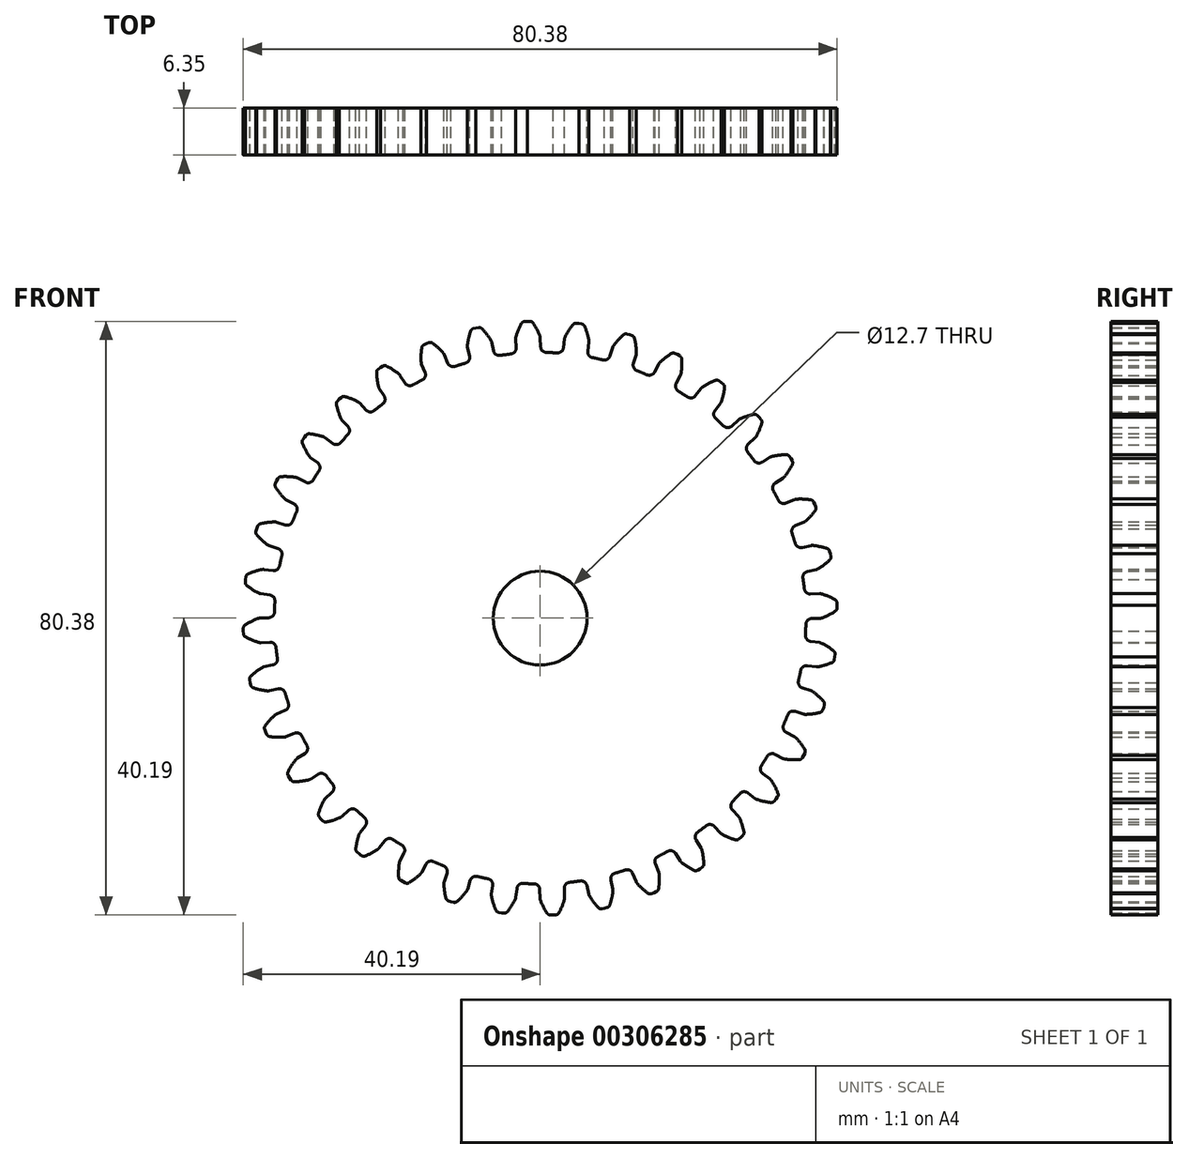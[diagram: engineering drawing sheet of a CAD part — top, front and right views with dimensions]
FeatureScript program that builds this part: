
annotation { "Feature Type Name" : "Feature", "Feature Type Description" : "" }
export const myFeature = defineFeature(function(context is Context, id is Id, definition is map)
    precondition{}
    {
        {
            var Q0;
            Q0=qCreatedBy(makeId("Front.planeOp"),FACE);
            var sketch = newSketch(context, id + "F0", { "sketchPlane" : qUnion([Q0])});
            skArc(sketch, "E0", {"start": v(-3.97, 35.76) * mm, "mid": v(1.57, -35.94) * mm, "end": v(0.84, 35.97) * mm});
            skArc(sketch, "E1.trimOffspring", {"start": v(-0.05, 38.23) * mm, "mid": v(-0.46, 39.12) * mm, "end": v(-0.95, 39.96) * mm});
            skLineSegment(sketch, "E2", {"start": v(-1.38, 40.2) * mm, "end": v(-1.75, 40.2) * mm});
            skLineSegment(sketch, "E3", {"start": v(0, 37.97) * mm, "end": v(0.06, 36.73) * mm});
            skLineSegment(sketch, "E4.MirrorCS", {"start": v(-2.13, 40.16) * mm, "end": v(-1.75, 40.2) * mm});
            skArc(sketch, "E5.MirrorCS", {"start": v(-3.28, 38.09) * mm, "mid": v(-2.96, 39.01) * mm, "end": v(-2.54, 39.9) * mm});
            skLineSegment(sketch, "E6.MirrorCS", {"start": v(-3.31, 37.82) * mm, "end": v(-3.26, 36.59) * mm});
            skPoint(sketch, "E7.visualSharp", {"position": v(-3.23, 35.83) * mm});
            skArc(sketch, "E7.filletArc", {"start": v(-3.97, 35.76) * mm, "mid": v(-3.45, 36.03) * mm, "end": v(-3.26, 36.59) * mm});
            skPoint(sketch, "E8.visualSharp", {"position": v(0.1, 35.98) * mm});
            skArc(sketch, "E8.filletArc", {"start": v(0.06, 36.73) * mm, "mid": v(0.3, 36.2) * mm, "end": v(0.84, 35.97) * mm});
            skPoint(sketch, "E9.visualSharp", {"position": v(0, 38.1) * mm});
            skArc(sketch, "E9.filletArc", {"start": v(0, 37.97) * mm, "mid": v(-0.01, 38.1) * mm, "end": v(-0.05, 38.23) * mm});
            skPoint(sketch, "E10.visualSharp", {"position": v(-3.32, 37.96) * mm});
            skArc(sketch, "E10.filletArc", {"start": v(-3.28, 38.09) * mm, "mid": v(-3.3, 37.96) * mm, "end": v(-3.31, 37.82) * mm});
            skPoint(sketch, "E11.visualSharp", {"position": v(-1.1, 40.2) * mm});
            skArc(sketch, "E11.filletArc", {"start": v(-0.95, 39.96) * mm, "mid": v(-1.13, 40.13) * mm, "end": v(-1.38, 40.2) * mm});
            skPoint(sketch, "E12.visualSharp", {"position": v(-2.4, 40.14) * mm});
            skArc(sketch, "E12.filletArc", {"start": v(-2.13, 40.16) * mm, "mid": v(-2.37, 40.08) * mm, "end": v(-2.54, 39.9) * mm});
            skLineSegment(sketch, "E13.1.0", {"start": v(-9.83, 36.67) * mm, "end": v(-9.57, 35.47) * mm});
            skArc(sketch, "E13.1.1", {"start": v(-9.85, 36.94) * mm, "mid": v(-9.68, 37.9) * mm, "end": v(-9.42, 38.85) * mm});
            skPoint(sketch, "E13.1.2", {"position": v(-6.16, 35.45) * mm});
            skLineSegment(sketch, "E13.1.3", {"start": v(-6.59, 37.4) * mm, "end": v(-6.32, 36.19) * mm});
            skPoint(sketch, "E13.1.4", {"position": v(-9.86, 36.8) * mm});
            skPoint(sketch, "E13.1.5", {"position": v(-9.4, 34.73) * mm});
            skPoint(sketch, "E13.1.6", {"position": v(-8.07, 39.4) * mm});
            skArc(sketch, "E13.1.7", {"start": v(-6.69, 37.64) * mm, "mid": v(-7.24, 38.45) * mm, "end": v(-7.88, 39.2) * mm});
            skPoint(sketch, "E13.1.8", {"position": v(-6.62, 37.52) * mm});
            skPoint(sketch, "E13.1.9", {"position": v(-9.33, 39.1) * mm});
            skArc(sketch, "E13.1.10", {"start": v(-6.32, 36.19) * mm, "mid": v(-6, 35.7) * mm, "end": v(-5.42, 35.57) * mm});
            skArc(sketch, "E13.1.11", {"start": v(-10.12, 34.53) * mm, "mid": v(-9.66, 34.89) * mm, "end": v(-9.57, 35.47) * mm});
            skArc(sketch, "E13.1.12", {"start": v(-7.88, 39.2) * mm, "mid": v(-8.09, 39.33) * mm, "end": v(-8.33, 39.34) * mm});
            skLineSegment(sketch, "E13.1.13", {"start": v(-8.33, 39.34) * mm, "end": v(-8.7, 39.28) * mm});
            skLineSegment(sketch, "E13.1.14", {"start": v(-9.07, 39.18) * mm, "end": v(-8.7, 39.28) * mm});
            skArc(sketch, "E13.1.15", {"start": v(-6.59, 37.4) * mm, "mid": v(-6.63, 37.52) * mm, "end": v(-6.69, 37.64) * mm});
            skArc(sketch, "E13.1.16", {"start": v(-9.85, 36.94) * mm, "mid": v(-9.85, 36.8) * mm, "end": v(-9.83, 36.67) * mm});
            skArc(sketch, "E13.1.17", {"start": v(-9.07, 39.18) * mm, "mid": v(-9.3, 39.06) * mm, "end": v(-9.42, 38.85) * mm});
            skLineSegment(sketch, "E13.2.0", {"start": v(-16.05, 34.4) * mm, "end": v(-15.58, 33.27) * mm});
            skArc(sketch, "E13.2.1", {"start": v(-16.11, 34.67) * mm, "mid": v(-16.12, 35.65) * mm, "end": v(-16.03, 36.62) * mm});
            skPoint(sketch, "E13.2.2", {"position": v(-12.22, 33.84) * mm});
            skLineSegment(sketch, "E13.2.3", {"start": v(-12.98, 35.68) * mm, "end": v(-12.5, 34.54) * mm});
            skPoint(sketch, "E13.2.4", {"position": v(-16.1, 34.53) * mm});
            skPoint(sketch, "E13.2.5", {"position": v(-15.29, 32.57) * mm});
            skPoint(sketch, "E13.2.6", {"position": v(-14.79, 37.4) * mm});
            skArc(sketch, "E13.2.7", {"start": v(-13.12, 35.9) * mm, "mid": v(-13.8, 36.6) * mm, "end": v(-14.56, 37.23) * mm});
            skPoint(sketch, "E13.2.8", {"position": v(-13.03, 35.8) * mm});
            skPoint(sketch, "E13.2.9", {"position": v(-15.98, 36.9) * mm});
            skArc(sketch, "E13.2.10", {"start": v(-12.5, 34.54) * mm, "mid": v(-12.1, 34.12) * mm, "end": v(-11.51, 34.09) * mm});
            skArc(sketch, "E13.2.11", {"start": v(-15.96, 32.24) * mm, "mid": v(-15.57, 32.68) * mm, "end": v(-15.58, 33.27) * mm});
            skArc(sketch, "E13.2.12", {"start": v(-14.56, 37.23) * mm, "mid": v(-14.8, 37.32) * mm, "end": v(-15.04, 37.3) * mm});
            skLineSegment(sketch, "E13.2.13", {"start": v(-15.04, 37.3) * mm, "end": v(-15.4, 37.17) * mm});
            skLineSegment(sketch, "E13.2.14", {"start": v(-15.74, 37) * mm, "end": v(-15.4, 37.17) * mm});
            skArc(sketch, "E13.2.15", {"start": v(-12.98, 35.68) * mm, "mid": v(-13.04, 35.8) * mm, "end": v(-13.12, 35.9) * mm});
            skArc(sketch, "E13.2.16", {"start": v(-16.11, 34.67) * mm, "mid": v(-16.1, 34.54) * mm, "end": v(-16.05, 34.4) * mm});
            skArc(sketch, "E13.2.17", {"start": v(-15.74, 37) * mm, "mid": v(-15.93, 36.85) * mm, "end": v(-16.03, 36.62) * mm});
            skLineSegment(sketch, "E13.3.0", {"start": v(-21.78, 31.1) * mm, "end": v(-21.12, 30.06) * mm});
            skArc(sketch, "E13.3.1", {"start": v(-21.89, 31.34) * mm, "mid": v(-22.06, 32.3) * mm, "end": v(-22.14, 33.28) * mm});
            skPoint(sketch, "E13.3.2", {"position": v(-17.9, 31.2) * mm});
            skLineSegment(sketch, "E13.3.3", {"start": v(-18.98, 32.88) * mm, "end": v(-18.32, 31.84) * mm});
            skPoint(sketch, "E13.3.4", {"position": v(-21.85, 31.2) * mm});
            skPoint(sketch, "E13.3.5", {"position": v(-20.71, 29.42) * mm});
            skPoint(sketch, "E13.3.6", {"position": v(-21.05, 34.25) * mm});
            skArc(sketch, "E13.3.7", {"start": v(-19.16, 33.08) * mm, "mid": v(-19.95, 33.65) * mm, "end": v(-20.8, 34.13) * mm});
            skPoint(sketch, "E13.3.8", {"position": v(-19.05, 33) * mm});
            skPoint(sketch, "E13.3.9", {"position": v(-22.15, 33.56) * mm});
            skArc(sketch, "E13.3.10", {"start": v(-18.32, 31.84) * mm, "mid": v(-17.84, 31.5) * mm, "end": v(-17.26, 31.57) * mm});
            skArc(sketch, "E13.3.11", {"start": v(-21.32, 28.98) * mm, "mid": v(-21, 29.48) * mm, "end": v(-21.12, 30.06) * mm});
            skArc(sketch, "E13.3.12", {"start": v(-20.8, 34.13) * mm, "mid": v(-21.05, 34.19) * mm, "end": v(-21.29, 34.12) * mm});
            skLineSegment(sketch, "E13.3.13", {"start": v(-21.29, 34.12) * mm, "end": v(-21.62, 33.93) * mm});
            skLineSegment(sketch, "E13.3.14", {"start": v(-21.93, 33.71) * mm, "end": v(-21.62, 33.93) * mm});
            skArc(sketch, "E13.3.15", {"start": v(-18.98, 32.88) * mm, "mid": v(-19.06, 33) * mm, "end": v(-19.16, 33.08) * mm});
            skArc(sketch, "E13.3.16", {"start": v(-21.89, 31.34) * mm, "mid": v(-21.84, 31.22) * mm, "end": v(-21.78, 31.1) * mm});
            skArc(sketch, "E13.3.17", {"start": v(-21.93, 33.71) * mm, "mid": v(-22.09, 33.52) * mm, "end": v(-22.14, 33.28) * mm});
            skLineSegment(sketch, "E13.4.0", {"start": v(-26.85, 26.84) * mm, "end": v(-26.02, 25.93) * mm});
            skArc(sketch, "E13.4.1", {"start": v(-27, 27.07) * mm, "mid": v(-27.34, 27.98) * mm, "end": v(-27.59, 28.93) * mm});
            skPoint(sketch, "E13.4.2", {"position": v(-23.06, 27.62) * mm});
            skLineSegment(sketch, "E13.4.3", {"start": v(-24.4, 29.09) * mm, "end": v(-23.57, 28.18) * mm});
            skPoint(sketch, "E13.4.4", {"position": v(-26.94, 26.94) * mm});
            skPoint(sketch, "E13.4.5", {"position": v(-25.5, 25.38) * mm});
            skPoint(sketch, "E13.4.6", {"position": v(-26.68, 30.08) * mm});
            skArc(sketch, "E13.4.7", {"start": v(-24.61, 29.25) * mm, "mid": v(-25.5, 29.67) * mm, "end": v(-26.42, 30) * mm});
            skPoint(sketch, "E13.4.8", {"position": v(-24.5, 29.19) * mm});
            skPoint(sketch, "E13.4.9", {"position": v(-27.64, 29.2) * mm});
            skArc(sketch, "E13.4.10", {"start": v(-23.57, 28.18) * mm, "mid": v(-23.04, 27.92) * mm, "end": v(-22.48, 28.1) * mm});
            skArc(sketch, "E13.4.11", {"start": v(-26.03, 24.84) * mm, "mid": v(-25.8, 25.38) * mm, "end": v(-26.02, 25.93) * mm});
            skArc(sketch, "E13.4.12", {"start": v(-26.42, 30) * mm, "mid": v(-26.67, 30.01) * mm, "end": v(-26.89, 29.9) * mm});
            skLineSegment(sketch, "E13.4.13", {"start": v(-26.89, 29.9) * mm, "end": v(-27.18, 29.66) * mm});
            skLineSegment(sketch, "E13.4.14", {"start": v(-27.45, 29.4) * mm, "end": v(-27.18, 29.66) * mm});
            skArc(sketch, "E13.4.15", {"start": v(-24.4, 29.09) * mm, "mid": v(-24.5, 29.18) * mm, "end": v(-24.61, 29.25) * mm});
            skArc(sketch, "E13.4.16", {"start": v(-27, 27.07) * mm, "mid": v(-26.93, 26.95) * mm, "end": v(-26.85, 26.84) * mm});
            skArc(sketch, "E13.4.17", {"start": v(-27.45, 29.4) * mm, "mid": v(-27.58, 29.18) * mm, "end": v(-27.59, 28.93) * mm});
            skLineSegment(sketch, "E13.5.0", {"start": v(-31.1, 21.77) * mm, "end": v(-30.13, 21.02) * mm});
            skArc(sketch, "E13.5.1", {"start": v(-31.29, 21.97) * mm, "mid": v(-31.78, 22.81) * mm, "end": v(-32.2, 23.7) * mm});
            skPoint(sketch, "E13.5.2", {"position": v(-27.5, 23.2) * mm});
            skLineSegment(sketch, "E13.5.3", {"start": v(-29.08, 24.41) * mm, "end": v(-28.1, 23.66) * mm});
            skPoint(sketch, "E13.5.4", {"position": v(-31.2, 21.85) * mm});
            skPoint(sketch, "E13.5.5", {"position": v(-29.53, 20.56) * mm});
            skPoint(sketch, "E13.5.6", {"position": v(-31.5, 24.99) * mm});
            skArc(sketch, "E13.5.7", {"start": v(-29.32, 24.53) * mm, "mid": v(-30.26, 24.8) * mm, "end": v(-31.23, 24.96) * mm});
            skPoint(sketch, "E13.5.8", {"position": v(-29.19, 24.5) * mm});
            skPoint(sketch, "E13.5.9", {"position": v(-32.29, 23.96) * mm});
            skArc(sketch, "E13.5.10", {"start": v(-28.1, 23.66) * mm, "mid": v(-27.54, 23.5) * mm, "end": v(-27.01, 23.76) * mm});
            skArc(sketch, "E13.5.11", {"start": v(-29.95, 19.94) * mm, "mid": v(-29.82, 20.52) * mm, "end": v(-30.13, 21.02) * mm});
            skArc(sketch, "E13.5.12", {"start": v(-31.23, 24.96) * mm, "mid": v(-31.47, 24.93) * mm, "end": v(-31.67, 24.78) * mm});
            skLineSegment(sketch, "E13.5.13", {"start": v(-31.67, 24.78) * mm, "end": v(-31.92, 24.5) * mm});
            skLineSegment(sketch, "E13.5.14", {"start": v(-32.14, 24.18) * mm, "end": v(-31.92, 24.5) * mm});
            skArc(sketch, "E13.5.15", {"start": v(-29.08, 24.41) * mm, "mid": v(-29.2, 24.48) * mm, "end": v(-29.32, 24.53) * mm});
            skArc(sketch, "E13.5.16", {"start": v(-31.29, 21.97) * mm, "mid": v(-31.2, 21.86) * mm, "end": v(-31.1, 21.77) * mm});
            skArc(sketch, "E13.5.17", {"start": v(-32.14, 24.18) * mm, "mid": v(-32.22, 23.95) * mm, "end": v(-32.2, 23.7) * mm});
            skLineSegment(sketch, "E13.6.0", {"start": v(-34.41, 16.04) * mm, "end": v(-33.32, 15.47) * mm});
            skArc(sketch, "E13.6.1", {"start": v(-34.63, 16.2) * mm, "mid": v(-35.26, 16.95) * mm, "end": v(-35.82, 17.75) * mm});
            skPoint(sketch, "E13.6.2", {"position": v(-31.11, 18.07) * mm});
            skLineSegment(sketch, "E13.6.3", {"start": v(-32.88, 18.99) * mm, "end": v(-31.78, 18.42) * mm});
            skPoint(sketch, "E13.6.4", {"position": v(-34.53, 16.1) * mm});
            skPoint(sketch, "E13.6.5", {"position": v(-32.65, 15.12) * mm});
            skPoint(sketch, "E13.6.6", {"position": v(-35.36, 19.14) * mm});
            skArc(sketch, "E13.6.7", {"start": v(-33.13, 19.07) * mm, "mid": v(-34.1, 19.17) * mm, "end": v(-35.09, 19.16) * mm});
            skPoint(sketch, "E13.6.8", {"position": v(-33, 19.05) * mm});
            skPoint(sketch, "E13.6.9", {"position": v(-35.96, 17.99) * mm});
            skArc(sketch, "E13.6.10", {"start": v(-31.78, 18.42) * mm, "mid": v(-31.2, 18.36) * mm, "end": v(-30.73, 18.71) * mm});
            skArc(sketch, "E13.6.11", {"start": v(-32.95, 14.44) * mm, "mid": v(-32.93, 15.03) * mm, "end": v(-33.32, 15.47) * mm});
            skArc(sketch, "E13.6.12", {"start": v(-35.09, 19.16) * mm, "mid": v(-35.32, 19.08) * mm, "end": v(-35.5, 18.9) * mm});
            skLineSegment(sketch, "E13.6.13", {"start": v(-35.5, 18.9) * mm, "end": v(-35.69, 18.58) * mm});
            skLineSegment(sketch, "E13.6.14", {"start": v(-35.85, 18.23) * mm, "end": v(-35.69, 18.58) * mm});
            skArc(sketch, "E13.6.15", {"start": v(-32.88, 18.99) * mm, "mid": v(-33, 19.04) * mm, "end": v(-33.13, 19.07) * mm});
            skArc(sketch, "E13.6.16", {"start": v(-34.63, 16.2) * mm, "mid": v(-34.53, 16.11) * mm, "end": v(-34.41, 16.04) * mm});
            skArc(sketch, "E13.6.17", {"start": v(-35.85, 18.23) * mm, "mid": v(-35.9, 17.99) * mm, "end": v(-35.82, 17.75) * mm});
            skLineSegment(sketch, "E13.7.0", {"start": v(-36.68, 9.82) * mm, "end": v(-35.5, 9.45) * mm});
            skArc(sketch, "E13.7.1", {"start": v(-36.91, 9.94) * mm, "mid": v(-37.67, 10.56) * mm, "end": v(-38.36, 11.26) * mm});
            skPoint(sketch, "E13.7.2", {"position": v(-33.78, 12.4) * mm});
            skLineSegment(sketch, "E13.7.3", {"start": v(-35.68, 13) * mm, "end": v(-34.5, 12.62) * mm});
            skPoint(sketch, "E13.7.4", {"position": v(-36.8, 9.86) * mm});
            skPoint(sketch, "E13.7.5", {"position": v(-34.78, 9.22) * mm});
            skPoint(sketch, "E13.7.6", {"position": v(-38.15, 12.7) * mm});
            skArc(sketch, "E13.7.7", {"start": v(-35.94, 13.03) * mm, "mid": v(-36.92, 12.95) * mm, "end": v(-37.88, 12.77) * mm});
            skPoint(sketch, "E13.7.8", {"position": v(-35.8, 13.03) * mm});
            skPoint(sketch, "E13.7.9", {"position": v(-38.54, 11.47) * mm});
            skArc(sketch, "E13.7.10", {"start": v(-34.5, 12.62) * mm, "mid": v(-33.91, 12.66) * mm, "end": v(-33.51, 13.1) * mm});
            skArc(sketch, "E13.7.11", {"start": v(-34.96, 8.5) * mm, "mid": v(-35.04, 9.08) * mm, "end": v(-35.5, 9.45) * mm});
            skArc(sketch, "E13.7.12", {"start": v(-37.88, 12.77) * mm, "mid": v(-38.1, 12.66) * mm, "end": v(-38.24, 12.45) * mm});
            skLineSegment(sketch, "E13.7.13", {"start": v(-38.24, 12.45) * mm, "end": v(-38.37, 12.1) * mm});
            skLineSegment(sketch, "E13.7.14", {"start": v(-38.47, 11.73) * mm, "end": v(-38.37, 12.1) * mm});
            skArc(sketch, "E13.7.15", {"start": v(-35.68, 13) * mm, "mid": v(-35.8, 13.02) * mm, "end": v(-35.94, 13.03) * mm});
            skArc(sketch, "E13.7.16", {"start": v(-36.91, 9.94) * mm, "mid": v(-36.8, 9.87) * mm, "end": v(-36.68, 9.82) * mm});
            skArc(sketch, "E13.7.17", {"start": v(-38.47, 11.73) * mm, "mid": v(-38.47, 11.48) * mm, "end": v(-38.36, 11.26) * mm});
            skLineSegment(sketch, "E13.8.0", {"start": v(-37.82, 3.3) * mm, "end": v(-36.6, 3.14) * mm});
            skArc(sketch, "E13.8.1", {"start": v(-38.08, 3.38) * mm, "mid": v(-38.93, 3.86) * mm, "end": v(-39.73, 4.43) * mm});
            skPoint(sketch, "E13.8.2", {"position": v(-35.42, 6.34) * mm});
            skLineSegment(sketch, "E13.8.3", {"start": v(-37.4, 6.6) * mm, "end": v(-36.17, 6.44) * mm});
            skPoint(sketch, "E13.8.4", {"position": v(-37.96, 3.32) * mm});
            skPoint(sketch, "E13.8.5", {"position": v(-35.85, 3.04) * mm});
            skPoint(sketch, "E13.8.6", {"position": v(-39.77, 5.89) * mm});
            skArc(sketch, "E13.8.7", {"start": v(-37.66, 6.59) * mm, "mid": v(-38.6, 6.34) * mm, "end": v(-39.52, 6) * mm});
            skPoint(sketch, "E13.8.8", {"position": v(-37.52, 6.62) * mm});
            skPoint(sketch, "E13.8.9", {"position": v(-39.94, 4.6) * mm});
            skArc(sketch, "E13.8.10", {"start": v(-36.17, 6.44) * mm, "mid": v(-35.6, 6.58) * mm, "end": v(-35.28, 7.07) * mm});
            skArc(sketch, "E13.8.11", {"start": v(-35.9, 2.3) * mm, "mid": v(-36.09, 2.86) * mm, "end": v(-36.6, 3.14) * mm});
            skArc(sketch, "E13.8.12", {"start": v(-39.52, 6) * mm, "mid": v(-39.72, 5.85) * mm, "end": v(-39.82, 5.62) * mm});
            skLineSegment(sketch, "E13.8.13", {"start": v(-39.82, 5.62) * mm, "end": v(-39.89, 5.25) * mm});
            skLineSegment(sketch, "E13.8.14", {"start": v(-39.92, 4.87) * mm, "end": v(-39.89, 5.25) * mm});
            skArc(sketch, "E13.8.15", {"start": v(-37.4, 6.6) * mm, "mid": v(-37.52, 6.6) * mm, "end": v(-37.66, 6.59) * mm});
            skArc(sketch, "E13.8.16", {"start": v(-38.08, 3.38) * mm, "mid": v(-37.95, 3.33) * mm, "end": v(-37.82, 3.3) * mm});
            skArc(sketch, "E13.8.17", {"start": v(-39.92, 4.87) * mm, "mid": v(-39.88, 4.63) * mm, "end": v(-39.73, 4.43) * mm});
            skLineSegment(sketch, "E13.9.0", {"start": v(-37.82, -3.31) * mm, "end": v(-36.59, -3.26) * mm});
            skArc(sketch, "E13.9.1", {"start": v(-38.09, -3.28) * mm, "mid": v(-39.01, -2.96) * mm, "end": v(-39.9, -2.54) * mm});
            skPoint(sketch, "E13.9.2", {"position": v(-35.98, 0.1) * mm});
            skLineSegment(sketch, "E13.9.3", {"start": v(-37.97, 0) * mm, "end": v(-36.73, 0.06) * mm});
            skPoint(sketch, "E13.9.4", {"position": v(-37.96, -3.32) * mm});
            skPoint(sketch, "E13.9.5", {"position": v(-35.83, -3.23) * mm});
            skPoint(sketch, "E13.9.6", {"position": v(-40.2, -1.1) * mm});
            skArc(sketch, "E13.9.7", {"start": v(-38.23, -0.05) * mm, "mid": v(-39.12, -0.46) * mm, "end": v(-39.96, -0.95) * mm});
            skPoint(sketch, "E13.9.8", {"position": v(-38.1, 0) * mm});
            skPoint(sketch, "E13.9.9", {"position": v(-40.14, -2.4) * mm});
            skArc(sketch, "E13.9.10", {"start": v(-36.73, 0.06) * mm, "mid": v(-36.2, 0.3) * mm, "end": v(-35.97, 0.84) * mm});
            skArc(sketch, "E13.9.11", {"start": v(-35.76, -3.97) * mm, "mid": v(-36.03, -3.45) * mm, "end": v(-36.59, -3.26) * mm});
            skArc(sketch, "E13.9.12", {"start": v(-39.96, -0.95) * mm, "mid": v(-40.13, -1.13) * mm, "end": v(-40.2, -1.38) * mm});
            skLineSegment(sketch, "E13.9.13", {"start": v(-40.2, -1.38) * mm, "end": v(-40.2, -1.75) * mm});
            skLineSegment(sketch, "E13.9.14", {"start": v(-40.16, -2.13) * mm, "end": v(-40.2, -1.75) * mm});
            skArc(sketch, "E13.9.15", {"start": v(-37.97, 0) * mm, "mid": v(-38.1, -0.01) * mm, "end": v(-38.23, -0.05) * mm});
            skArc(sketch, "E13.9.16", {"start": v(-38.09, -3.28) * mm, "mid": v(-37.96, -3.3) * mm, "end": v(-37.82, -3.31) * mm});
            skArc(sketch, "E13.9.17", {"start": v(-40.16, -2.13) * mm, "mid": v(-40.08, -2.37) * mm, "end": v(-39.9, -2.54) * mm});
            skLineSegment(sketch, "E13.10.0", {"start": v(-36.67, -9.83) * mm, "end": v(-35.47, -9.57) * mm});
            skArc(sketch, "E13.10.1", {"start": v(-36.94, -9.85) * mm, "mid": v(-37.9, -9.68) * mm, "end": v(-38.85, -9.42) * mm});
            skPoint(sketch, "E13.10.2", {"position": v(-35.45, -6.16) * mm});
            skLineSegment(sketch, "E13.10.3", {"start": v(-37.4, -6.59) * mm, "end": v(-36.19, -6.32) * mm});
            skPoint(sketch, "E13.10.4", {"position": v(-36.8, -9.86) * mm});
            skPoint(sketch, "E13.10.5", {"position": v(-34.73, -9.4) * mm});
            skPoint(sketch, "E13.10.6", {"position": v(-39.4, -8.07) * mm});
            skArc(sketch, "E13.10.7", {"start": v(-37.64, -6.69) * mm, "mid": v(-38.45, -7.24) * mm, "end": v(-39.2, -7.88) * mm});
            skPoint(sketch, "E13.10.8", {"position": v(-37.52, -6.62) * mm});
            skPoint(sketch, "E13.10.9", {"position": v(-39.1, -9.33) * mm});
            skArc(sketch, "E13.10.10", {"start": v(-36.19, -6.32) * mm, "mid": v(-35.7, -6) * mm, "end": v(-35.57, -5.42) * mm});
            skArc(sketch, "E13.10.11", {"start": v(-34.53, -10.12) * mm, "mid": v(-34.89, -9.66) * mm, "end": v(-35.47, -9.57) * mm});
            skArc(sketch, "E13.10.12", {"start": v(-39.2, -7.88) * mm, "mid": v(-39.33, -8.09) * mm, "end": v(-39.34, -8.33) * mm});
            skLineSegment(sketch, "E13.10.13", {"start": v(-39.34, -8.33) * mm, "end": v(-39.28, -8.7) * mm});
            skLineSegment(sketch, "E13.10.14", {"start": v(-39.18, -9.07) * mm, "end": v(-39.28, -8.7) * mm});
            skArc(sketch, "E13.10.15", {"start": v(-37.4, -6.59) * mm, "mid": v(-37.52, -6.63) * mm, "end": v(-37.64, -6.69) * mm});
            skArc(sketch, "E13.10.16", {"start": v(-36.94, -9.85) * mm, "mid": v(-36.8, -9.85) * mm, "end": v(-36.67, -9.83) * mm});
            skArc(sketch, "E13.10.17", {"start": v(-39.18, -9.07) * mm, "mid": v(-39.06, -9.3) * mm, "end": v(-38.85, -9.42) * mm});
            skLineSegment(sketch, "E13.11.0", {"start": v(-34.4, -16.05) * mm, "end": v(-33.27, -15.58) * mm});
            skArc(sketch, "E13.11.1", {"start": v(-34.67, -16.11) * mm, "mid": v(-35.65, -16.12) * mm, "end": v(-36.62, -16.03) * mm});
            skPoint(sketch, "E13.11.2", {"position": v(-33.84, -12.22) * mm});
            skLineSegment(sketch, "E13.11.3", {"start": v(-35.68, -12.98) * mm, "end": v(-34.54, -12.5) * mm});
            skPoint(sketch, "E13.11.4", {"position": v(-34.53, -16.1) * mm});
            skPoint(sketch, "E13.11.5", {"position": v(-32.57, -15.29) * mm});
            skPoint(sketch, "E13.11.6", {"position": v(-37.4, -14.79) * mm});
            skArc(sketch, "E13.11.7", {"start": v(-35.9, -13.12) * mm, "mid": v(-36.6, -13.8) * mm, "end": v(-37.23, -14.56) * mm});
            skPoint(sketch, "E13.11.8", {"position": v(-35.8, -13.03) * mm});
            skPoint(sketch, "E13.11.9", {"position": v(-36.9, -15.98) * mm});
            skArc(sketch, "E13.11.10", {"start": v(-34.54, -12.5) * mm, "mid": v(-34.12, -12.1) * mm, "end": v(-34.09, -11.51) * mm});
            skArc(sketch, "E13.11.11", {"start": v(-32.24, -15.96) * mm, "mid": v(-32.68, -15.57) * mm, "end": v(-33.27, -15.58) * mm});
            skArc(sketch, "E13.11.12", {"start": v(-37.23, -14.56) * mm, "mid": v(-37.32, -14.8) * mm, "end": v(-37.3, -15.04) * mm});
            skLineSegment(sketch, "E13.11.13", {"start": v(-37.3, -15.04) * mm, "end": v(-37.17, -15.4) * mm});
            skLineSegment(sketch, "E13.11.14", {"start": v(-37, -15.74) * mm, "end": v(-37.17, -15.4) * mm});
            skArc(sketch, "E13.11.15", {"start": v(-35.68, -12.98) * mm, "mid": v(-35.8, -13.04) * mm, "end": v(-35.9, -13.12) * mm});
            skArc(sketch, "E13.11.16", {"start": v(-34.67, -16.11) * mm, "mid": v(-34.54, -16.1) * mm, "end": v(-34.4, -16.05) * mm});
            skArc(sketch, "E13.11.17", {"start": v(-37, -15.74) * mm, "mid": v(-36.85, -15.93) * mm, "end": v(-36.62, -16.03) * mm});
            skLineSegment(sketch, "E13.12.0", {"start": v(-31.1, -21.78) * mm, "end": v(-30.06, -21.12) * mm});
            skArc(sketch, "E13.12.1", {"start": v(-31.34, -21.89) * mm, "mid": v(-32.3, -22.06) * mm, "end": v(-33.28, -22.14) * mm});
            skPoint(sketch, "E13.12.2", {"position": v(-31.2, -17.9) * mm});
            skLineSegment(sketch, "E13.12.3", {"start": v(-32.88, -18.98) * mm, "end": v(-31.84, -18.32) * mm});
            skPoint(sketch, "E13.12.4", {"position": v(-31.2, -21.85) * mm});
            skPoint(sketch, "E13.12.5", {"position": v(-29.42, -20.71) * mm});
            skPoint(sketch, "E13.12.6", {"position": v(-34.25, -21.05) * mm});
            skArc(sketch, "E13.12.7", {"start": v(-33.08, -19.16) * mm, "mid": v(-33.65, -19.95) * mm, "end": v(-34.13, -20.8) * mm});
            skPoint(sketch, "E13.12.8", {"position": v(-33, -19.05) * mm});
            skPoint(sketch, "E13.12.9", {"position": v(-33.56, -22.15) * mm});
            skArc(sketch, "E13.12.10", {"start": v(-31.84, -18.32) * mm, "mid": v(-31.5, -17.84) * mm, "end": v(-31.57, -17.26) * mm});
            skArc(sketch, "E13.12.11", {"start": v(-28.98, -21.32) * mm, "mid": v(-29.48, -21) * mm, "end": v(-30.06, -21.12) * mm});
            skArc(sketch, "E13.12.12", {"start": v(-34.13, -20.8) * mm, "mid": v(-34.19, -21.05) * mm, "end": v(-34.12, -21.29) * mm});
            skLineSegment(sketch, "E13.12.13", {"start": v(-34.12, -21.29) * mm, "end": v(-33.93, -21.62) * mm});
            skLineSegment(sketch, "E13.12.14", {"start": v(-33.71, -21.93) * mm, "end": v(-33.93, -21.62) * mm});
            skArc(sketch, "E13.12.15", {"start": v(-32.88, -18.98) * mm, "mid": v(-33, -19.06) * mm, "end": v(-33.08, -19.16) * mm});
            skArc(sketch, "E13.12.16", {"start": v(-31.34, -21.89) * mm, "mid": v(-31.22, -21.84) * mm, "end": v(-31.1, -21.78) * mm});
            skArc(sketch, "E13.12.17", {"start": v(-33.71, -21.93) * mm, "mid": v(-33.52, -22.09) * mm, "end": v(-33.28, -22.14) * mm});
            skLineSegment(sketch, "E13.13.0", {"start": v(-26.84, -26.85) * mm, "end": v(-25.93, -26.02) * mm});
            skArc(sketch, "E13.13.1", {"start": v(-27.07, -27) * mm, "mid": v(-27.98, -27.34) * mm, "end": v(-28.93, -27.59) * mm});
            skPoint(sketch, "E13.13.2", {"position": v(-27.62, -23.06) * mm});
            skLineSegment(sketch, "E13.13.3", {"start": v(-29.09, -24.4) * mm, "end": v(-28.18, -23.57) * mm});
            skPoint(sketch, "E13.13.4", {"position": v(-26.94, -26.94) * mm});
            skPoint(sketch, "E13.13.5", {"position": v(-25.38, -25.5) * mm});
            skPoint(sketch, "E13.13.6", {"position": v(-30.08, -26.68) * mm});
            skArc(sketch, "E13.13.7", {"start": v(-29.25, -24.61) * mm, "mid": v(-29.67, -25.5) * mm, "end": v(-30, -26.42) * mm});
            skPoint(sketch, "E13.13.8", {"position": v(-29.19, -24.5) * mm});
            skPoint(sketch, "E13.13.9", {"position": v(-29.2, -27.64) * mm});
            skArc(sketch, "E13.13.10", {"start": v(-28.18, -23.57) * mm, "mid": v(-27.92, -23.04) * mm, "end": v(-28.1, -22.48) * mm});
            skArc(sketch, "E13.13.11", {"start": v(-24.84, -26.03) * mm, "mid": v(-25.38, -25.8) * mm, "end": v(-25.93, -26.02) * mm});
            skArc(sketch, "E13.13.12", {"start": v(-30, -26.42) * mm, "mid": v(-30.01, -26.67) * mm, "end": v(-29.9, -26.89) * mm});
            skLineSegment(sketch, "E13.13.13", {"start": v(-29.9, -26.89) * mm, "end": v(-29.66, -27.18) * mm});
            skLineSegment(sketch, "E13.13.14", {"start": v(-29.4, -27.45) * mm, "end": v(-29.66, -27.18) * mm});
            skArc(sketch, "E13.13.15", {"start": v(-29.09, -24.4) * mm, "mid": v(-29.18, -24.5) * mm, "end": v(-29.25, -24.61) * mm});
            skArc(sketch, "E13.13.16", {"start": v(-27.07, -27) * mm, "mid": v(-26.95, -26.93) * mm, "end": v(-26.84, -26.85) * mm});
            skArc(sketch, "E13.13.17", {"start": v(-29.4, -27.45) * mm, "mid": v(-29.18, -27.58) * mm, "end": v(-28.93, -27.59) * mm});
            skLineSegment(sketch, "E13.14.0", {"start": v(-21.77, -31.1) * mm, "end": v(-21.02, -30.13) * mm});
            skArc(sketch, "E13.14.1", {"start": v(-21.97, -31.29) * mm, "mid": v(-22.81, -31.78) * mm, "end": v(-23.7, -32.2) * mm});
            skPoint(sketch, "E13.14.2", {"position": v(-23.2, -27.5) * mm});
            skLineSegment(sketch, "E13.14.3", {"start": v(-24.41, -29.08) * mm, "end": v(-23.66, -28.1) * mm});
            skPoint(sketch, "E13.14.4", {"position": v(-21.85, -31.2) * mm});
            skPoint(sketch, "E13.14.5", {"position": v(-20.56, -29.53) * mm});
            skPoint(sketch, "E13.14.6", {"position": v(-24.99, -31.5) * mm});
            skArc(sketch, "E13.14.7", {"start": v(-24.53, -29.32) * mm, "mid": v(-24.8, -30.26) * mm, "end": v(-24.96, -31.23) * mm});
            skPoint(sketch, "E13.14.8", {"position": v(-24.5, -29.19) * mm});
            skPoint(sketch, "E13.14.9", {"position": v(-23.96, -32.29) * mm});
            skArc(sketch, "E13.14.10", {"start": v(-23.66, -28.1) * mm, "mid": v(-23.5, -27.54) * mm, "end": v(-23.76, -27.01) * mm});
            skArc(sketch, "E13.14.11", {"start": v(-19.94, -29.95) * mm, "mid": v(-20.52, -29.82) * mm, "end": v(-21.02, -30.13) * mm});
            skArc(sketch, "E13.14.12", {"start": v(-24.96, -31.23) * mm, "mid": v(-24.93, -31.47) * mm, "end": v(-24.78, -31.67) * mm});
            skLineSegment(sketch, "E13.14.13", {"start": v(-24.78, -31.67) * mm, "end": v(-24.5, -31.92) * mm});
            skLineSegment(sketch, "E13.14.14", {"start": v(-24.18, -32.14) * mm, "end": v(-24.5, -31.92) * mm});
            skArc(sketch, "E13.14.15", {"start": v(-24.41, -29.08) * mm, "mid": v(-24.48, -29.2) * mm, "end": v(-24.53, -29.32) * mm});
            skArc(sketch, "E13.14.16", {"start": v(-21.97, -31.29) * mm, "mid": v(-21.86, -31.2) * mm, "end": v(-21.77, -31.1) * mm});
            skArc(sketch, "E13.14.17", {"start": v(-24.18, -32.14) * mm, "mid": v(-23.95, -32.22) * mm, "end": v(-23.7, -32.2) * mm});
            skLineSegment(sketch, "E13.15.0", {"start": v(-16.04, -34.41) * mm, "end": v(-15.47, -33.32) * mm});
            skArc(sketch, "E13.15.1", {"start": v(-16.2, -34.63) * mm, "mid": v(-16.95, -35.26) * mm, "end": v(-17.75, -35.82) * mm});
            skPoint(sketch, "E13.15.2", {"position": v(-18.07, -31.11) * mm});
            skLineSegment(sketch, "E13.15.3", {"start": v(-18.99, -32.88) * mm, "end": v(-18.42, -31.78) * mm});
            skPoint(sketch, "E13.15.4", {"position": v(-16.1, -34.53) * mm});
            skPoint(sketch, "E13.15.5", {"position": v(-15.12, -32.65) * mm});
            skPoint(sketch, "E13.15.6", {"position": v(-19.14, -35.36) * mm});
            skArc(sketch, "E13.15.7", {"start": v(-19.07, -33.13) * mm, "mid": v(-19.17, -34.1) * mm, "end": v(-19.16, -35.09) * mm});
            skPoint(sketch, "E13.15.8", {"position": v(-19.05, -33) * mm});
            skPoint(sketch, "E13.15.9", {"position": v(-17.99, -35.96) * mm});
            skArc(sketch, "E13.15.10", {"start": v(-18.42, -31.78) * mm, "mid": v(-18.36, -31.2) * mm, "end": v(-18.71, -30.73) * mm});
            skArc(sketch, "E13.15.11", {"start": v(-14.44, -32.95) * mm, "mid": v(-15.03, -32.93) * mm, "end": v(-15.47, -33.32) * mm});
            skArc(sketch, "E13.15.12", {"start": v(-19.16, -35.09) * mm, "mid": v(-19.08, -35.32) * mm, "end": v(-18.9, -35.5) * mm});
            skLineSegment(sketch, "E13.15.13", {"start": v(-18.9, -35.5) * mm, "end": v(-18.58, -35.69) * mm});
            skLineSegment(sketch, "E13.15.14", {"start": v(-18.23, -35.85) * mm, "end": v(-18.58, -35.69) * mm});
            skArc(sketch, "E13.15.15", {"start": v(-18.99, -32.88) * mm, "mid": v(-19.04, -33) * mm, "end": v(-19.07, -33.13) * mm});
            skArc(sketch, "E13.15.16", {"start": v(-16.2, -34.63) * mm, "mid": v(-16.11, -34.53) * mm, "end": v(-16.04, -34.41) * mm});
            skArc(sketch, "E13.15.17", {"start": v(-18.23, -35.85) * mm, "mid": v(-17.99, -35.9) * mm, "end": v(-17.75, -35.82) * mm});
            skLineSegment(sketch, "E13.16.0", {"start": v(-9.82, -36.68) * mm, "end": v(-9.45, -35.5) * mm});
            skArc(sketch, "E13.16.1", {"start": v(-9.94, -36.91) * mm, "mid": v(-10.56, -37.67) * mm, "end": v(-11.26, -38.36) * mm});
            skPoint(sketch, "E13.16.2", {"position": v(-12.4, -33.78) * mm});
            skLineSegment(sketch, "E13.16.3", {"start": v(-13, -35.68) * mm, "end": v(-12.62, -34.5) * mm});
            skPoint(sketch, "E13.16.4", {"position": v(-9.86, -36.8) * mm});
            skPoint(sketch, "E13.16.5", {"position": v(-9.22, -34.78) * mm});
            skPoint(sketch, "E13.16.6", {"position": v(-12.7, -38.15) * mm});
            skArc(sketch, "E13.16.7", {"start": v(-13.03, -35.94) * mm, "mid": v(-12.95, -36.92) * mm, "end": v(-12.77, -37.88) * mm});
            skPoint(sketch, "E13.16.8", {"position": v(-13.03, -35.8) * mm});
            skPoint(sketch, "E13.16.9", {"position": v(-11.47, -38.54) * mm});
            skArc(sketch, "E13.16.10", {"start": v(-12.62, -34.5) * mm, "mid": v(-12.66, -33.91) * mm, "end": v(-13.1, -33.51) * mm});
            skArc(sketch, "E13.16.11", {"start": v(-8.5, -34.96) * mm, "mid": v(-9.08, -35.04) * mm, "end": v(-9.45, -35.5) * mm});
            skArc(sketch, "E13.16.12", {"start": v(-12.77, -37.88) * mm, "mid": v(-12.66, -38.1) * mm, "end": v(-12.45, -38.24) * mm});
            skLineSegment(sketch, "E13.16.13", {"start": v(-12.45, -38.24) * mm, "end": v(-12.1, -38.37) * mm});
            skLineSegment(sketch, "E13.16.14", {"start": v(-11.73, -38.47) * mm, "end": v(-12.1, -38.37) * mm});
            skArc(sketch, "E13.16.15", {"start": v(-13, -35.68) * mm, "mid": v(-13.02, -35.8) * mm, "end": v(-13.03, -35.94) * mm});
            skArc(sketch, "E13.16.16", {"start": v(-9.94, -36.91) * mm, "mid": v(-9.87, -36.8) * mm, "end": v(-9.82, -36.68) * mm});
            skArc(sketch, "E13.16.17", {"start": v(-11.73, -38.47) * mm, "mid": v(-11.48, -38.47) * mm, "end": v(-11.26, -38.36) * mm});
            skLineSegment(sketch, "E13.17.0", {"start": v(-3.3, -37.82) * mm, "end": v(-3.14, -36.6) * mm});
            skArc(sketch, "E13.17.1", {"start": v(-3.38, -38.08) * mm, "mid": v(-3.86, -38.93) * mm, "end": v(-4.43, -39.73) * mm});
            skPoint(sketch, "E13.17.2", {"position": v(-6.34, -35.42) * mm});
            skLineSegment(sketch, "E13.17.3", {"start": v(-6.6, -37.4) * mm, "end": v(-6.44, -36.17) * mm});
            skPoint(sketch, "E13.17.4", {"position": v(-3.32, -37.96) * mm});
            skPoint(sketch, "E13.17.5", {"position": v(-3.04, -35.85) * mm});
            skPoint(sketch, "E13.17.6", {"position": v(-5.89, -39.77) * mm});
            skArc(sketch, "E13.17.7", {"start": v(-6.59, -37.66) * mm, "mid": v(-6.34, -38.6) * mm, "end": v(-6, -39.52) * mm});
            skPoint(sketch, "E13.17.8", {"position": v(-6.62, -37.52) * mm});
            skPoint(sketch, "E13.17.9", {"position": v(-4.6, -39.94) * mm});
            skArc(sketch, "E13.17.10", {"start": v(-6.44, -36.17) * mm, "mid": v(-6.58, -35.6) * mm, "end": v(-7.07, -35.28) * mm});
            skArc(sketch, "E13.17.11", {"start": v(-2.3, -35.9) * mm, "mid": v(-2.86, -36.09) * mm, "end": v(-3.14, -36.6) * mm});
            skArc(sketch, "E13.17.12", {"start": v(-6, -39.52) * mm, "mid": v(-5.85, -39.72) * mm, "end": v(-5.62, -39.82) * mm});
            skLineSegment(sketch, "E13.17.13", {"start": v(-5.62, -39.82) * mm, "end": v(-5.25, -39.89) * mm});
            skLineSegment(sketch, "E13.17.14", {"start": v(-4.87, -39.92) * mm, "end": v(-5.25, -39.89) * mm});
            skArc(sketch, "E13.17.15", {"start": v(-6.6, -37.4) * mm, "mid": v(-6.6, -37.52) * mm, "end": v(-6.59, -37.66) * mm});
            skArc(sketch, "E13.17.16", {"start": v(-3.38, -38.08) * mm, "mid": v(-3.33, -37.95) * mm, "end": v(-3.3, -37.82) * mm});
            skArc(sketch, "E13.17.17", {"start": v(-4.87, -39.92) * mm, "mid": v(-4.63, -39.88) * mm, "end": v(-4.43, -39.73) * mm});
            skLineSegment(sketch, "E13.18.0", {"start": v(3.31, -37.82) * mm, "end": v(3.26, -36.59) * mm});
            skArc(sketch, "E13.18.1", {"start": v(3.28, -38.09) * mm, "mid": v(2.96, -39.01) * mm, "end": v(2.54, -39.9) * mm});
            skPoint(sketch, "E13.18.2", {"position": v(-0.1, -35.98) * mm});
            skLineSegment(sketch, "E13.18.3", {"start": v(0, -37.97) * mm, "end": v(-0.06, -36.73) * mm});
            skPoint(sketch, "E13.18.4", {"position": v(3.32, -37.96) * mm});
            skPoint(sketch, "E13.18.5", {"position": v(3.23, -35.83) * mm});
            skPoint(sketch, "E13.18.6", {"position": v(1.1, -40.2) * mm});
            skArc(sketch, "E13.18.7", {"start": v(0.05, -38.23) * mm, "mid": v(0.46, -39.12) * mm, "end": v(0.95, -39.96) * mm});
            skPoint(sketch, "E13.18.8", {"position": v(0, -38.1) * mm});
            skPoint(sketch, "E13.18.9", {"position": v(2.4, -40.14) * mm});
            skArc(sketch, "E13.18.10", {"start": v(-0.06, -36.73) * mm, "mid": v(-0.3, -36.2) * mm, "end": v(-0.84, -35.97) * mm});
            skArc(sketch, "E13.18.11", {"start": v(3.97, -35.76) * mm, "mid": v(3.45, -36.03) * mm, "end": v(3.26, -36.59) * mm});
            skArc(sketch, "E13.18.12", {"start": v(0.95, -39.96) * mm, "mid": v(1.13, -40.13) * mm, "end": v(1.38, -40.2) * mm});
            skLineSegment(sketch, "E13.18.13", {"start": v(1.38, -40.2) * mm, "end": v(1.75, -40.2) * mm});
            skLineSegment(sketch, "E13.18.14", {"start": v(2.13, -40.16) * mm, "end": v(1.75, -40.2) * mm});
            skArc(sketch, "E13.18.15", {"start": v(0, -37.97) * mm, "mid": v(0.01, -38.1) * mm, "end": v(0.05, -38.23) * mm});
            skArc(sketch, "E13.18.16", {"start": v(3.28, -38.09) * mm, "mid": v(3.3, -37.96) * mm, "end": v(3.31, -37.82) * mm});
            skArc(sketch, "E13.18.17", {"start": v(2.13, -40.16) * mm, "mid": v(2.37, -40.08) * mm, "end": v(2.54, -39.9) * mm});
            skLineSegment(sketch, "E13.19.0", {"start": v(9.83, -36.67) * mm, "end": v(9.57, -35.47) * mm});
            skArc(sketch, "E13.19.1", {"start": v(9.85, -36.94) * mm, "mid": v(9.68, -37.9) * mm, "end": v(9.42, -38.85) * mm});
            skPoint(sketch, "E13.19.2", {"position": v(6.16, -35.45) * mm});
            skLineSegment(sketch, "E13.19.3", {"start": v(6.59, -37.4) * mm, "end": v(6.32, -36.19) * mm});
            skPoint(sketch, "E13.19.4", {"position": v(9.86, -36.8) * mm});
            skPoint(sketch, "E13.19.5", {"position": v(9.4, -34.73) * mm});
            skPoint(sketch, "E13.19.6", {"position": v(8.07, -39.4) * mm});
            skArc(sketch, "E13.19.7", {"start": v(6.69, -37.64) * mm, "mid": v(7.24, -38.45) * mm, "end": v(7.88, -39.2) * mm});
            skPoint(sketch, "E13.19.8", {"position": v(6.62, -37.52) * mm});
            skPoint(sketch, "E13.19.9", {"position": v(9.33, -39.1) * mm});
            skArc(sketch, "E13.19.10", {"start": v(6.32, -36.19) * mm, "mid": v(6, -35.7) * mm, "end": v(5.42, -35.57) * mm});
            skArc(sketch, "E13.19.11", {"start": v(10.12, -34.53) * mm, "mid": v(9.66, -34.89) * mm, "end": v(9.57, -35.47) * mm});
            skArc(sketch, "E13.19.12", {"start": v(7.88, -39.2) * mm, "mid": v(8.09, -39.33) * mm, "end": v(8.33, -39.34) * mm});
            skLineSegment(sketch, "E13.19.13", {"start": v(8.33, -39.34) * mm, "end": v(8.7, -39.28) * mm});
            skLineSegment(sketch, "E13.19.14", {"start": v(9.07, -39.18) * mm, "end": v(8.7, -39.28) * mm});
            skArc(sketch, "E13.19.15", {"start": v(6.59, -37.4) * mm, "mid": v(6.63, -37.52) * mm, "end": v(6.69, -37.64) * mm});
            skArc(sketch, "E13.19.16", {"start": v(9.85, -36.94) * mm, "mid": v(9.85, -36.8) * mm, "end": v(9.83, -36.67) * mm});
            skArc(sketch, "E13.19.17", {"start": v(9.07, -39.18) * mm, "mid": v(9.3, -39.06) * mm, "end": v(9.42, -38.85) * mm});
            skLineSegment(sketch, "E13.20.0", {"start": v(16.05, -34.4) * mm, "end": v(15.58, -33.27) * mm});
            skArc(sketch, "E13.20.1", {"start": v(16.11, -34.67) * mm, "mid": v(16.12, -35.65) * mm, "end": v(16.03, -36.62) * mm});
            skPoint(sketch, "E13.20.2", {"position": v(12.22, -33.84) * mm});
            skLineSegment(sketch, "E13.20.3", {"start": v(12.98, -35.68) * mm, "end": v(12.5, -34.54) * mm});
            skPoint(sketch, "E13.20.4", {"position": v(16.1, -34.53) * mm});
            skPoint(sketch, "E13.20.5", {"position": v(15.29, -32.57) * mm});
            skPoint(sketch, "E13.20.6", {"position": v(14.79, -37.4) * mm});
            skArc(sketch, "E13.20.7", {"start": v(13.12, -35.9) * mm, "mid": v(13.8, -36.6) * mm, "end": v(14.56, -37.23) * mm});
            skPoint(sketch, "E13.20.8", {"position": v(13.03, -35.8) * mm});
            skPoint(sketch, "E13.20.9", {"position": v(15.98, -36.9) * mm});
            skArc(sketch, "E13.20.10", {"start": v(12.5, -34.54) * mm, "mid": v(12.1, -34.12) * mm, "end": v(11.51, -34.09) * mm});
            skArc(sketch, "E13.20.11", {"start": v(15.96, -32.24) * mm, "mid": v(15.57, -32.68) * mm, "end": v(15.58, -33.27) * mm});
            skArc(sketch, "E13.20.12", {"start": v(14.56, -37.23) * mm, "mid": v(14.8, -37.32) * mm, "end": v(15.04, -37.3) * mm});
            skLineSegment(sketch, "E13.20.13", {"start": v(15.04, -37.3) * mm, "end": v(15.4, -37.17) * mm});
            skLineSegment(sketch, "E13.20.14", {"start": v(15.74, -37) * mm, "end": v(15.4, -37.17) * mm});
            skArc(sketch, "E13.20.15", {"start": v(12.98, -35.68) * mm, "mid": v(13.04, -35.8) * mm, "end": v(13.12, -35.9) * mm});
            skArc(sketch, "E13.20.16", {"start": v(16.11, -34.67) * mm, "mid": v(16.1, -34.54) * mm, "end": v(16.05, -34.4) * mm});
            skArc(sketch, "E13.20.17", {"start": v(15.74, -37) * mm, "mid": v(15.93, -36.85) * mm, "end": v(16.03, -36.62) * mm});
            skLineSegment(sketch, "E13.21.0", {"start": v(21.78, -31.1) * mm, "end": v(21.12, -30.06) * mm});
            skArc(sketch, "E13.21.1", {"start": v(21.89, -31.34) * mm, "mid": v(22.06, -32.3) * mm, "end": v(22.14, -33.28) * mm});
            skPoint(sketch, "E13.21.2", {"position": v(17.9, -31.2) * mm});
            skLineSegment(sketch, "E13.21.3", {"start": v(18.98, -32.88) * mm, "end": v(18.32, -31.84) * mm});
            skPoint(sketch, "E13.21.4", {"position": v(21.85, -31.2) * mm});
            skPoint(sketch, "E13.21.5", {"position": v(20.71, -29.42) * mm});
            skPoint(sketch, "E13.21.6", {"position": v(21.05, -34.25) * mm});
            skArc(sketch, "E13.21.7", {"start": v(19.16, -33.08) * mm, "mid": v(19.95, -33.65) * mm, "end": v(20.8, -34.13) * mm});
            skPoint(sketch, "E13.21.8", {"position": v(19.05, -33) * mm});
            skPoint(sketch, "E13.21.9", {"position": v(22.15, -33.56) * mm});
            skArc(sketch, "E13.21.10", {"start": v(18.32, -31.84) * mm, "mid": v(17.84, -31.5) * mm, "end": v(17.26, -31.57) * mm});
            skArc(sketch, "E13.21.11", {"start": v(21.32, -28.98) * mm, "mid": v(21, -29.48) * mm, "end": v(21.12, -30.06) * mm});
            skArc(sketch, "E13.21.12", {"start": v(20.8, -34.13) * mm, "mid": v(21.05, -34.19) * mm, "end": v(21.29, -34.12) * mm});
            skLineSegment(sketch, "E13.21.13", {"start": v(21.29, -34.12) * mm, "end": v(21.62, -33.93) * mm});
            skLineSegment(sketch, "E13.21.14", {"start": v(21.93, -33.71) * mm, "end": v(21.62, -33.93) * mm});
            skArc(sketch, "E13.21.15", {"start": v(18.98, -32.88) * mm, "mid": v(19.06, -33) * mm, "end": v(19.16, -33.08) * mm});
            skArc(sketch, "E13.21.16", {"start": v(21.89, -31.34) * mm, "mid": v(21.84, -31.22) * mm, "end": v(21.78, -31.1) * mm});
            skArc(sketch, "E13.21.17", {"start": v(21.93, -33.71) * mm, "mid": v(22.09, -33.52) * mm, "end": v(22.14, -33.28) * mm});
            skLineSegment(sketch, "E13.22.0", {"start": v(26.85, -26.84) * mm, "end": v(26.02, -25.93) * mm});
            skArc(sketch, "E13.22.1", {"start": v(27, -27.07) * mm, "mid": v(27.34, -27.98) * mm, "end": v(27.59, -28.93) * mm});
            skPoint(sketch, "E13.22.2", {"position": v(23.06, -27.62) * mm});
            skLineSegment(sketch, "E13.22.3", {"start": v(24.4, -29.09) * mm, "end": v(23.57, -28.18) * mm});
            skPoint(sketch, "E13.22.4", {"position": v(26.94, -26.94) * mm});
            skPoint(sketch, "E13.22.5", {"position": v(25.5, -25.38) * mm});
            skPoint(sketch, "E13.22.6", {"position": v(26.68, -30.08) * mm});
            skArc(sketch, "E13.22.7", {"start": v(24.61, -29.25) * mm, "mid": v(25.5, -29.67) * mm, "end": v(26.42, -30) * mm});
            skPoint(sketch, "E13.22.8", {"position": v(24.5, -29.19) * mm});
            skPoint(sketch, "E13.22.9", {"position": v(27.64, -29.2) * mm});
            skArc(sketch, "E13.22.10", {"start": v(23.57, -28.18) * mm, "mid": v(23.04, -27.92) * mm, "end": v(22.48, -28.1) * mm});
            skArc(sketch, "E13.22.11", {"start": v(26.03, -24.84) * mm, "mid": v(25.8, -25.38) * mm, "end": v(26.02, -25.93) * mm});
            skArc(sketch, "E13.22.12", {"start": v(26.42, -30) * mm, "mid": v(26.67, -30.01) * mm, "end": v(26.89, -29.9) * mm});
            skLineSegment(sketch, "E13.22.13", {"start": v(26.89, -29.9) * mm, "end": v(27.18, -29.66) * mm});
            skLineSegment(sketch, "E13.22.14", {"start": v(27.45, -29.4) * mm, "end": v(27.18, -29.66) * mm});
            skArc(sketch, "E13.22.15", {"start": v(24.4, -29.09) * mm, "mid": v(24.5, -29.18) * mm, "end": v(24.61, -29.25) * mm});
            skArc(sketch, "E13.22.16", {"start": v(27, -27.07) * mm, "mid": v(26.93, -26.95) * mm, "end": v(26.85, -26.84) * mm});
            skArc(sketch, "E13.22.17", {"start": v(27.45, -29.4) * mm, "mid": v(27.58, -29.18) * mm, "end": v(27.59, -28.93) * mm});
            skLineSegment(sketch, "E13.23.0", {"start": v(31.1, -21.77) * mm, "end": v(30.13, -21.02) * mm});
            skArc(sketch, "E13.23.1", {"start": v(31.29, -21.97) * mm, "mid": v(31.78, -22.81) * mm, "end": v(32.2, -23.7) * mm});
            skPoint(sketch, "E13.23.2", {"position": v(27.5, -23.2) * mm});
            skLineSegment(sketch, "E13.23.3", {"start": v(29.08, -24.41) * mm, "end": v(28.1, -23.66) * mm});
            skPoint(sketch, "E13.23.4", {"position": v(31.2, -21.85) * mm});
            skPoint(sketch, "E13.23.5", {"position": v(29.53, -20.56) * mm});
            skPoint(sketch, "E13.23.6", {"position": v(31.5, -24.99) * mm});
            skArc(sketch, "E13.23.7", {"start": v(29.32, -24.53) * mm, "mid": v(30.26, -24.8) * mm, "end": v(31.23, -24.96) * mm});
            skPoint(sketch, "E13.23.8", {"position": v(29.19, -24.5) * mm});
            skPoint(sketch, "E13.23.9", {"position": v(32.29, -23.96) * mm});
            skArc(sketch, "E13.23.10", {"start": v(28.1, -23.66) * mm, "mid": v(27.54, -23.5) * mm, "end": v(27.01, -23.76) * mm});
            skArc(sketch, "E13.23.11", {"start": v(29.95, -19.94) * mm, "mid": v(29.82, -20.52) * mm, "end": v(30.13, -21.02) * mm});
            skArc(sketch, "E13.23.12", {"start": v(31.23, -24.96) * mm, "mid": v(31.47, -24.93) * mm, "end": v(31.67, -24.78) * mm});
            skLineSegment(sketch, "E13.23.13", {"start": v(31.67, -24.78) * mm, "end": v(31.92, -24.5) * mm});
            skLineSegment(sketch, "E13.23.14", {"start": v(32.14, -24.18) * mm, "end": v(31.92, -24.5) * mm});
            skArc(sketch, "E13.23.15", {"start": v(29.08, -24.41) * mm, "mid": v(29.2, -24.48) * mm, "end": v(29.32, -24.53) * mm});
            skArc(sketch, "E13.23.16", {"start": v(31.29, -21.97) * mm, "mid": v(31.2, -21.86) * mm, "end": v(31.1, -21.77) * mm});
            skArc(sketch, "E13.23.17", {"start": v(32.14, -24.18) * mm, "mid": v(32.22, -23.95) * mm, "end": v(32.2, -23.7) * mm});
            skLineSegment(sketch, "E13.24.0", {"start": v(34.41, -16.04) * mm, "end": v(33.32, -15.47) * mm});
            skArc(sketch, "E13.24.1", {"start": v(34.63, -16.2) * mm, "mid": v(35.26, -16.95) * mm, "end": v(35.82, -17.75) * mm});
            skPoint(sketch, "E13.24.2", {"position": v(31.11, -18.07) * mm});
            skLineSegment(sketch, "E13.24.3", {"start": v(32.88, -18.99) * mm, "end": v(31.78, -18.42) * mm});
            skPoint(sketch, "E13.24.4", {"position": v(34.53, -16.1) * mm});
            skPoint(sketch, "E13.24.5", {"position": v(32.65, -15.12) * mm});
            skPoint(sketch, "E13.24.6", {"position": v(35.36, -19.14) * mm});
            skArc(sketch, "E13.24.7", {"start": v(33.13, -19.07) * mm, "mid": v(34.1, -19.17) * mm, "end": v(35.09, -19.16) * mm});
            skPoint(sketch, "E13.24.8", {"position": v(33, -19.05) * mm});
            skPoint(sketch, "E13.24.9", {"position": v(35.96, -17.99) * mm});
            skArc(sketch, "E13.24.10", {"start": v(31.78, -18.42) * mm, "mid": v(31.2, -18.36) * mm, "end": v(30.73, -18.71) * mm});
            skArc(sketch, "E13.24.11", {"start": v(32.95, -14.44) * mm, "mid": v(32.93, -15.03) * mm, "end": v(33.32, -15.47) * mm});
            skArc(sketch, "E13.24.12", {"start": v(35.09, -19.16) * mm, "mid": v(35.32, -19.08) * mm, "end": v(35.5, -18.9) * mm});
            skLineSegment(sketch, "E13.24.13", {"start": v(35.5, -18.9) * mm, "end": v(35.69, -18.58) * mm});
            skLineSegment(sketch, "E13.24.14", {"start": v(35.85, -18.23) * mm, "end": v(35.69, -18.58) * mm});
            skArc(sketch, "E13.24.15", {"start": v(32.88, -18.99) * mm, "mid": v(33, -19.04) * mm, "end": v(33.13, -19.07) * mm});
            skArc(sketch, "E13.24.16", {"start": v(34.63, -16.2) * mm, "mid": v(34.53, -16.11) * mm, "end": v(34.41, -16.04) * mm});
            skArc(sketch, "E13.24.17", {"start": v(35.85, -18.23) * mm, "mid": v(35.9, -17.99) * mm, "end": v(35.82, -17.75) * mm});
            skLineSegment(sketch, "E13.25.0", {"start": v(36.68, -9.82) * mm, "end": v(35.5, -9.45) * mm});
            skArc(sketch, "E13.25.1", {"start": v(36.91, -9.94) * mm, "mid": v(37.67, -10.56) * mm, "end": v(38.36, -11.26) * mm});
            skPoint(sketch, "E13.25.2", {"position": v(33.78, -12.4) * mm});
            skLineSegment(sketch, "E13.25.3", {"start": v(35.68, -13) * mm, "end": v(34.5, -12.62) * mm});
            skPoint(sketch, "E13.25.4", {"position": v(36.8, -9.86) * mm});
            skPoint(sketch, "E13.25.5", {"position": v(34.78, -9.22) * mm});
            skPoint(sketch, "E13.25.6", {"position": v(38.15, -12.7) * mm});
            skArc(sketch, "E13.25.7", {"start": v(35.94, -13.03) * mm, "mid": v(36.92, -12.95) * mm, "end": v(37.88, -12.77) * mm});
            skPoint(sketch, "E13.25.8", {"position": v(35.8, -13.03) * mm});
            skPoint(sketch, "E13.25.9", {"position": v(38.54, -11.47) * mm});
            skArc(sketch, "E13.25.10", {"start": v(34.5, -12.62) * mm, "mid": v(33.91, -12.66) * mm, "end": v(33.51, -13.1) * mm});
            skArc(sketch, "E13.25.11", {"start": v(34.96, -8.5) * mm, "mid": v(35.04, -9.08) * mm, "end": v(35.5, -9.45) * mm});
            skArc(sketch, "E13.25.12", {"start": v(37.88, -12.77) * mm, "mid": v(38.1, -12.66) * mm, "end": v(38.24, -12.45) * mm});
            skLineSegment(sketch, "E13.25.13", {"start": v(38.24, -12.45) * mm, "end": v(38.37, -12.1) * mm});
            skLineSegment(sketch, "E13.25.14", {"start": v(38.47, -11.73) * mm, "end": v(38.37, -12.1) * mm});
            skArc(sketch, "E13.25.15", {"start": v(35.68, -13) * mm, "mid": v(35.8, -13.02) * mm, "end": v(35.94, -13.03) * mm});
            skArc(sketch, "E13.25.16", {"start": v(36.91, -9.94) * mm, "mid": v(36.8, -9.87) * mm, "end": v(36.68, -9.82) * mm});
            skArc(sketch, "E13.25.17", {"start": v(38.47, -11.73) * mm, "mid": v(38.47, -11.48) * mm, "end": v(38.36, -11.26) * mm});
            skLineSegment(sketch, "E13.26.0", {"start": v(37.82, -3.3) * mm, "end": v(36.6, -3.14) * mm});
            skArc(sketch, "E13.26.1", {"start": v(38.08, -3.38) * mm, "mid": v(38.93, -3.86) * mm, "end": v(39.73, -4.43) * mm});
            skPoint(sketch, "E13.26.2", {"position": v(35.42, -6.34) * mm});
            skLineSegment(sketch, "E13.26.3", {"start": v(37.4, -6.6) * mm, "end": v(36.17, -6.44) * mm});
            skPoint(sketch, "E13.26.4", {"position": v(37.96, -3.32) * mm});
            skPoint(sketch, "E13.26.5", {"position": v(35.85, -3.04) * mm});
            skPoint(sketch, "E13.26.6", {"position": v(39.77, -5.89) * mm});
            skArc(sketch, "E13.26.7", {"start": v(37.66, -6.59) * mm, "mid": v(38.6, -6.34) * mm, "end": v(39.52, -6) * mm});
            skPoint(sketch, "E13.26.8", {"position": v(37.52, -6.62) * mm});
            skPoint(sketch, "E13.26.9", {"position": v(39.94, -4.6) * mm});
            skArc(sketch, "E13.26.10", {"start": v(36.17, -6.44) * mm, "mid": v(35.6, -6.58) * mm, "end": v(35.28, -7.07) * mm});
            skArc(sketch, "E13.26.11", {"start": v(35.9, -2.3) * mm, "mid": v(36.09, -2.86) * mm, "end": v(36.6, -3.14) * mm});
            skArc(sketch, "E13.26.12", {"start": v(39.52, -6) * mm, "mid": v(39.72, -5.85) * mm, "end": v(39.82, -5.62) * mm});
            skLineSegment(sketch, "E13.26.13", {"start": v(39.82, -5.62) * mm, "end": v(39.89, -5.25) * mm});
            skLineSegment(sketch, "E13.26.14", {"start": v(39.92, -4.87) * mm, "end": v(39.89, -5.25) * mm});
            skArc(sketch, "E13.26.15", {"start": v(37.4, -6.6) * mm, "mid": v(37.52, -6.6) * mm, "end": v(37.66, -6.59) * mm});
            skArc(sketch, "E13.26.16", {"start": v(38.08, -3.38) * mm, "mid": v(37.95, -3.33) * mm, "end": v(37.82, -3.3) * mm});
            skArc(sketch, "E13.26.17", {"start": v(39.92, -4.87) * mm, "mid": v(39.88, -4.63) * mm, "end": v(39.73, -4.43) * mm});
            skLineSegment(sketch, "E13.27.0", {"start": v(37.82, 3.31) * mm, "end": v(36.59, 3.26) * mm});
            skArc(sketch, "E13.27.1", {"start": v(38.09, 3.28) * mm, "mid": v(39.01, 2.96) * mm, "end": v(39.9, 2.54) * mm});
            skPoint(sketch, "E13.27.2", {"position": v(35.98, -0.1) * mm});
            skLineSegment(sketch, "E13.27.3", {"start": v(37.97, 0) * mm, "end": v(36.73, -0.06) * mm});
            skPoint(sketch, "E13.27.4", {"position": v(37.96, 3.32) * mm});
            skPoint(sketch, "E13.27.5", {"position": v(35.83, 3.23) * mm});
            skPoint(sketch, "E13.27.6", {"position": v(40.2, 1.1) * mm});
            skArc(sketch, "E13.27.7", {"start": v(38.23, 0.05) * mm, "mid": v(39.12, 0.46) * mm, "end": v(39.96, 0.95) * mm});
            skPoint(sketch, "E13.27.8", {"position": v(38.1, 0) * mm});
            skPoint(sketch, "E13.27.9", {"position": v(40.14, 2.4) * mm});
            skArc(sketch, "E13.27.10", {"start": v(36.73, -0.06) * mm, "mid": v(36.2, -0.3) * mm, "end": v(35.97, -0.84) * mm});
            skArc(sketch, "E13.27.11", {"start": v(35.76, 3.97) * mm, "mid": v(36.03, 3.45) * mm, "end": v(36.59, 3.26) * mm});
            skArc(sketch, "E13.27.12", {"start": v(39.96, 0.95) * mm, "mid": v(40.13, 1.13) * mm, "end": v(40.2, 1.38) * mm});
            skLineSegment(sketch, "E13.27.13", {"start": v(40.2, 1.38) * mm, "end": v(40.2, 1.75) * mm});
            skLineSegment(sketch, "E13.27.14", {"start": v(40.16, 2.13) * mm, "end": v(40.2, 1.75) * mm});
            skArc(sketch, "E13.27.15", {"start": v(37.97, 0) * mm, "mid": v(38.1, 0.01) * mm, "end": v(38.23, 0.05) * mm});
            skArc(sketch, "E13.27.16", {"start": v(38.09, 3.28) * mm, "mid": v(37.96, 3.3) * mm, "end": v(37.82, 3.31) * mm});
            skArc(sketch, "E13.27.17", {"start": v(40.16, 2.13) * mm, "mid": v(40.08, 2.37) * mm, "end": v(39.9, 2.54) * mm});
            skLineSegment(sketch, "E13.28.0", {"start": v(36.67, 9.83) * mm, "end": v(35.47, 9.57) * mm});
            skArc(sketch, "E13.28.1", {"start": v(36.94, 9.85) * mm, "mid": v(37.9, 9.68) * mm, "end": v(38.85, 9.42) * mm});
            skPoint(sketch, "E13.28.2", {"position": v(35.45, 6.16) * mm});
            skLineSegment(sketch, "E13.28.3", {"start": v(37.4, 6.59) * mm, "end": v(36.19, 6.32) * mm});
            skPoint(sketch, "E13.28.4", {"position": v(36.8, 9.86) * mm});
            skPoint(sketch, "E13.28.5", {"position": v(34.73, 9.4) * mm});
            skPoint(sketch, "E13.28.6", {"position": v(39.4, 8.07) * mm});
            skArc(sketch, "E13.28.7", {"start": v(37.64, 6.69) * mm, "mid": v(38.45, 7.24) * mm, "end": v(39.2, 7.88) * mm});
            skPoint(sketch, "E13.28.8", {"position": v(37.52, 6.62) * mm});
            skPoint(sketch, "E13.28.9", {"position": v(39.1, 9.33) * mm});
            skArc(sketch, "E13.28.10", {"start": v(36.19, 6.32) * mm, "mid": v(35.7, 6) * mm, "end": v(35.57, 5.42) * mm});
            skArc(sketch, "E13.28.11", {"start": v(34.53, 10.12) * mm, "mid": v(34.89, 9.66) * mm, "end": v(35.47, 9.57) * mm});
            skArc(sketch, "E13.28.12", {"start": v(39.2, 7.88) * mm, "mid": v(39.33, 8.09) * mm, "end": v(39.34, 8.33) * mm});
            skLineSegment(sketch, "E13.28.13", {"start": v(39.34, 8.33) * mm, "end": v(39.28, 8.7) * mm});
            skLineSegment(sketch, "E13.28.14", {"start": v(39.18, 9.07) * mm, "end": v(39.28, 8.7) * mm});
            skArc(sketch, "E13.28.15", {"start": v(37.4, 6.59) * mm, "mid": v(37.52, 6.63) * mm, "end": v(37.64, 6.69) * mm});
            skArc(sketch, "E13.28.16", {"start": v(36.94, 9.85) * mm, "mid": v(36.8, 9.85) * mm, "end": v(36.67, 9.83) * mm});
            skArc(sketch, "E13.28.17", {"start": v(39.18, 9.07) * mm, "mid": v(39.06, 9.3) * mm, "end": v(38.85, 9.42) * mm});
            skLineSegment(sketch, "E13.29.0", {"start": v(34.4, 16.05) * mm, "end": v(33.27, 15.58) * mm});
            skArc(sketch, "E13.29.1", {"start": v(34.67, 16.11) * mm, "mid": v(35.65, 16.12) * mm, "end": v(36.62, 16.03) * mm});
            skPoint(sketch, "E13.29.2", {"position": v(33.84, 12.22) * mm});
            skLineSegment(sketch, "E13.29.3", {"start": v(35.68, 12.98) * mm, "end": v(34.54, 12.5) * mm});
            skPoint(sketch, "E13.29.4", {"position": v(34.53, 16.1) * mm});
            skPoint(sketch, "E13.29.5", {"position": v(32.57, 15.29) * mm});
            skPoint(sketch, "E13.29.6", {"position": v(37.4, 14.79) * mm});
            skArc(sketch, "E13.29.7", {"start": v(35.9, 13.12) * mm, "mid": v(36.6, 13.8) * mm, "end": v(37.23, 14.56) * mm});
            skPoint(sketch, "E13.29.8", {"position": v(35.8, 13.03) * mm});
            skPoint(sketch, "E13.29.9", {"position": v(36.9, 15.98) * mm});
            skArc(sketch, "E13.29.10", {"start": v(34.54, 12.5) * mm, "mid": v(34.12, 12.1) * mm, "end": v(34.09, 11.51) * mm});
            skArc(sketch, "E13.29.11", {"start": v(32.24, 15.96) * mm, "mid": v(32.68, 15.57) * mm, "end": v(33.27, 15.58) * mm});
            skArc(sketch, "E13.29.12", {"start": v(37.23, 14.56) * mm, "mid": v(37.32, 14.8) * mm, "end": v(37.3, 15.04) * mm});
            skLineSegment(sketch, "E13.29.13", {"start": v(37.3, 15.04) * mm, "end": v(37.17, 15.4) * mm});
            skLineSegment(sketch, "E13.29.14", {"start": v(37, 15.74) * mm, "end": v(37.17, 15.4) * mm});
            skArc(sketch, "E13.29.15", {"start": v(35.68, 12.98) * mm, "mid": v(35.8, 13.04) * mm, "end": v(35.9, 13.12) * mm});
            skArc(sketch, "E13.29.16", {"start": v(34.67, 16.11) * mm, "mid": v(34.54, 16.1) * mm, "end": v(34.4, 16.05) * mm});
            skArc(sketch, "E13.29.17", {"start": v(37, 15.74) * mm, "mid": v(36.85, 15.93) * mm, "end": v(36.62, 16.03) * mm});
            skLineSegment(sketch, "E13.30.0", {"start": v(31.1, 21.78) * mm, "end": v(30.06, 21.12) * mm});
            skArc(sketch, "E13.30.1", {"start": v(31.34, 21.89) * mm, "mid": v(32.3, 22.06) * mm, "end": v(33.28, 22.14) * mm});
            skPoint(sketch, "E13.30.2", {"position": v(31.2, 17.9) * mm});
            skLineSegment(sketch, "E13.30.3", {"start": v(32.88, 18.98) * mm, "end": v(31.84, 18.32) * mm});
            skPoint(sketch, "E13.30.4", {"position": v(31.2, 21.85) * mm});
            skPoint(sketch, "E13.30.5", {"position": v(29.42, 20.71) * mm});
            skPoint(sketch, "E13.30.6", {"position": v(34.25, 21.05) * mm});
            skArc(sketch, "E13.30.7", {"start": v(33.08, 19.16) * mm, "mid": v(33.65, 19.95) * mm, "end": v(34.13, 20.8) * mm});
            skPoint(sketch, "E13.30.8", {"position": v(33, 19.05) * mm});
            skPoint(sketch, "E13.30.9", {"position": v(33.56, 22.15) * mm});
            skArc(sketch, "E13.30.10", {"start": v(31.84, 18.32) * mm, "mid": v(31.5, 17.84) * mm, "end": v(31.57, 17.26) * mm});
            skArc(sketch, "E13.30.11", {"start": v(28.98, 21.32) * mm, "mid": v(29.48, 21) * mm, "end": v(30.06, 21.12) * mm});
            skArc(sketch, "E13.30.12", {"start": v(34.13, 20.8) * mm, "mid": v(34.19, 21.05) * mm, "end": v(34.12, 21.29) * mm});
            skLineSegment(sketch, "E13.30.13", {"start": v(34.12, 21.29) * mm, "end": v(33.93, 21.62) * mm});
            skLineSegment(sketch, "E13.30.14", {"start": v(33.71, 21.93) * mm, "end": v(33.93, 21.62) * mm});
            skArc(sketch, "E13.30.15", {"start": v(32.88, 18.98) * mm, "mid": v(33, 19.06) * mm, "end": v(33.08, 19.16) * mm});
            skArc(sketch, "E13.30.16", {"start": v(31.34, 21.89) * mm, "mid": v(31.22, 21.84) * mm, "end": v(31.1, 21.78) * mm});
            skArc(sketch, "E13.30.17", {"start": v(33.71, 21.93) * mm, "mid": v(33.52, 22.09) * mm, "end": v(33.28, 22.14) * mm});
            skLineSegment(sketch, "E13.31.0", {"start": v(26.84, 26.85) * mm, "end": v(25.93, 26.02) * mm});
            skArc(sketch, "E13.31.1", {"start": v(27.07, 27) * mm, "mid": v(27.98, 27.34) * mm, "end": v(28.93, 27.59) * mm});
            skPoint(sketch, "E13.31.2", {"position": v(27.62, 23.06) * mm});
            skLineSegment(sketch, "E13.31.3", {"start": v(29.09, 24.4) * mm, "end": v(28.18, 23.57) * mm});
            skPoint(sketch, "E13.31.4", {"position": v(26.94, 26.94) * mm});
            skPoint(sketch, "E13.31.5", {"position": v(25.38, 25.5) * mm});
            skPoint(sketch, "E13.31.6", {"position": v(30.08, 26.68) * mm});
            skArc(sketch, "E13.31.7", {"start": v(29.25, 24.61) * mm, "mid": v(29.67, 25.5) * mm, "end": v(30, 26.42) * mm});
            skPoint(sketch, "E13.31.8", {"position": v(29.19, 24.5) * mm});
            skPoint(sketch, "E13.31.9", {"position": v(29.2, 27.64) * mm});
            skArc(sketch, "E13.31.10", {"start": v(28.18, 23.57) * mm, "mid": v(27.92, 23.04) * mm, "end": v(28.1, 22.48) * mm});
            skArc(sketch, "E13.31.11", {"start": v(24.84, 26.03) * mm, "mid": v(25.38, 25.8) * mm, "end": v(25.93, 26.02) * mm});
            skArc(sketch, "E13.31.12", {"start": v(30, 26.42) * mm, "mid": v(30.01, 26.67) * mm, "end": v(29.9, 26.89) * mm});
            skLineSegment(sketch, "E13.31.13", {"start": v(29.9, 26.89) * mm, "end": v(29.66, 27.18) * mm});
            skLineSegment(sketch, "E13.31.14", {"start": v(29.4, 27.45) * mm, "end": v(29.66, 27.18) * mm});
            skArc(sketch, "E13.31.15", {"start": v(29.09, 24.4) * mm, "mid": v(29.18, 24.5) * mm, "end": v(29.25, 24.61) * mm});
            skArc(sketch, "E13.31.16", {"start": v(27.07, 27) * mm, "mid": v(26.95, 26.93) * mm, "end": v(26.84, 26.85) * mm});
            skArc(sketch, "E13.31.17", {"start": v(29.4, 27.45) * mm, "mid": v(29.18, 27.58) * mm, "end": v(28.93, 27.59) * mm});
            skLineSegment(sketch, "E13.32.0", {"start": v(21.77, 31.1) * mm, "end": v(21.02, 30.13) * mm});
            skArc(sketch, "E13.32.1", {"start": v(21.97, 31.29) * mm, "mid": v(22.81, 31.78) * mm, "end": v(23.7, 32.2) * mm});
            skPoint(sketch, "E13.32.2", {"position": v(23.2, 27.5) * mm});
            skLineSegment(sketch, "E13.32.3", {"start": v(24.41, 29.08) * mm, "end": v(23.66, 28.1) * mm});
            skPoint(sketch, "E13.32.4", {"position": v(21.85, 31.2) * mm});
            skPoint(sketch, "E13.32.5", {"position": v(20.56, 29.53) * mm});
            skPoint(sketch, "E13.32.6", {"position": v(24.99, 31.5) * mm});
            skArc(sketch, "E13.32.7", {"start": v(24.53, 29.32) * mm, "mid": v(24.8, 30.26) * mm, "end": v(24.96, 31.23) * mm});
            skPoint(sketch, "E13.32.8", {"position": v(24.5, 29.19) * mm});
            skPoint(sketch, "E13.32.9", {"position": v(23.96, 32.29) * mm});
            skArc(sketch, "E13.32.10", {"start": v(23.66, 28.1) * mm, "mid": v(23.5, 27.54) * mm, "end": v(23.76, 27.01) * mm});
            skArc(sketch, "E13.32.11", {"start": v(19.94, 29.95) * mm, "mid": v(20.52, 29.82) * mm, "end": v(21.02, 30.13) * mm});
            skArc(sketch, "E13.32.12", {"start": v(24.96, 31.23) * mm, "mid": v(24.93, 31.47) * mm, "end": v(24.78, 31.67) * mm});
            skLineSegment(sketch, "E13.32.13", {"start": v(24.78, 31.67) * mm, "end": v(24.5, 31.92) * mm});
            skLineSegment(sketch, "E13.32.14", {"start": v(24.18, 32.14) * mm, "end": v(24.5, 31.92) * mm});
            skArc(sketch, "E13.32.15", {"start": v(24.41, 29.08) * mm, "mid": v(24.48, 29.2) * mm, "end": v(24.53, 29.32) * mm});
            skArc(sketch, "E13.32.16", {"start": v(21.97, 31.29) * mm, "mid": v(21.86, 31.2) * mm, "end": v(21.77, 31.1) * mm});
            skArc(sketch, "E13.32.17", {"start": v(24.18, 32.14) * mm, "mid": v(23.95, 32.22) * mm, "end": v(23.7, 32.2) * mm});
            skLineSegment(sketch, "E13.33.0", {"start": v(16.04, 34.41) * mm, "end": v(15.47, 33.32) * mm});
            skArc(sketch, "E13.33.1", {"start": v(16.2, 34.63) * mm, "mid": v(16.95, 35.26) * mm, "end": v(17.75, 35.82) * mm});
            skPoint(sketch, "E13.33.2", {"position": v(18.07, 31.11) * mm});
            skLineSegment(sketch, "E13.33.3", {"start": v(18.99, 32.88) * mm, "end": v(18.42, 31.78) * mm});
            skPoint(sketch, "E13.33.4", {"position": v(16.1, 34.53) * mm});
            skPoint(sketch, "E13.33.5", {"position": v(15.12, 32.65) * mm});
            skPoint(sketch, "E13.33.6", {"position": v(19.14, 35.36) * mm});
            skArc(sketch, "E13.33.7", {"start": v(19.07, 33.13) * mm, "mid": v(19.17, 34.1) * mm, "end": v(19.16, 35.09) * mm});
            skPoint(sketch, "E13.33.8", {"position": v(19.05, 33) * mm});
            skPoint(sketch, "E13.33.9", {"position": v(17.99, 35.96) * mm});
            skArc(sketch, "E13.33.10", {"start": v(18.42, 31.78) * mm, "mid": v(18.36, 31.2) * mm, "end": v(18.71, 30.73) * mm});
            skArc(sketch, "E13.33.11", {"start": v(14.44, 32.95) * mm, "mid": v(15.03, 32.93) * mm, "end": v(15.47, 33.32) * mm});
            skArc(sketch, "E13.33.12", {"start": v(19.16, 35.09) * mm, "mid": v(19.08, 35.32) * mm, "end": v(18.9, 35.5) * mm});
            skLineSegment(sketch, "E13.33.13", {"start": v(18.9, 35.5) * mm, "end": v(18.58, 35.69) * mm});
            skLineSegment(sketch, "E13.33.14", {"start": v(18.23, 35.85) * mm, "end": v(18.58, 35.69) * mm});
            skArc(sketch, "E13.33.15", {"start": v(18.99, 32.88) * mm, "mid": v(19.04, 33) * mm, "end": v(19.07, 33.13) * mm});
            skArc(sketch, "E13.33.16", {"start": v(16.2, 34.63) * mm, "mid": v(16.11, 34.53) * mm, "end": v(16.04, 34.41) * mm});
            skArc(sketch, "E13.33.17", {"start": v(18.23, 35.85) * mm, "mid": v(17.99, 35.9) * mm, "end": v(17.75, 35.82) * mm});
            skLineSegment(sketch, "E13.34.0", {"start": v(9.82, 36.68) * mm, "end": v(9.45, 35.5) * mm});
            skArc(sketch, "E13.34.1", {"start": v(9.94, 36.91) * mm, "mid": v(10.56, 37.67) * mm, "end": v(11.26, 38.36) * mm});
            skPoint(sketch, "E13.34.2", {"position": v(12.4, 33.78) * mm});
            skLineSegment(sketch, "E13.34.3", {"start": v(13, 35.68) * mm, "end": v(12.62, 34.5) * mm});
            skPoint(sketch, "E13.34.4", {"position": v(9.86, 36.8) * mm});
            skPoint(sketch, "E13.34.5", {"position": v(9.22, 34.78) * mm});
            skPoint(sketch, "E13.34.6", {"position": v(12.7, 38.15) * mm});
            skArc(sketch, "E13.34.7", {"start": v(13.03, 35.94) * mm, "mid": v(12.95, 36.92) * mm, "end": v(12.77, 37.88) * mm});
            skPoint(sketch, "E13.34.8", {"position": v(13.03, 35.8) * mm});
            skPoint(sketch, "E13.34.9", {"position": v(11.47, 38.54) * mm});
            skArc(sketch, "E13.34.10", {"start": v(12.62, 34.5) * mm, "mid": v(12.66, 33.91) * mm, "end": v(13.1, 33.51) * mm});
            skArc(sketch, "E13.34.11", {"start": v(8.5, 34.96) * mm, "mid": v(9.08, 35.04) * mm, "end": v(9.45, 35.5) * mm});
            skArc(sketch, "E13.34.12", {"start": v(12.77, 37.88) * mm, "mid": v(12.66, 38.1) * mm, "end": v(12.45, 38.24) * mm});
            skLineSegment(sketch, "E13.34.13", {"start": v(12.45, 38.24) * mm, "end": v(12.1, 38.37) * mm});
            skLineSegment(sketch, "E13.34.14", {"start": v(11.73, 38.47) * mm, "end": v(12.1, 38.37) * mm});
            skArc(sketch, "E13.34.15", {"start": v(13, 35.68) * mm, "mid": v(13.02, 35.8) * mm, "end": v(13.03, 35.94) * mm});
            skArc(sketch, "E13.34.16", {"start": v(9.94, 36.91) * mm, "mid": v(9.87, 36.8) * mm, "end": v(9.82, 36.68) * mm});
            skArc(sketch, "E13.34.17", {"start": v(11.73, 38.47) * mm, "mid": v(11.48, 38.47) * mm, "end": v(11.26, 38.36) * mm});
            skLineSegment(sketch, "E13.35.0", {"start": v(3.3, 37.82) * mm, "end": v(3.14, 36.6) * mm});
            skArc(sketch, "E13.35.1", {"start": v(3.38, 38.08) * mm, "mid": v(3.86, 38.93) * mm, "end": v(4.43, 39.73) * mm});
            skPoint(sketch, "E13.35.2", {"position": v(6.34, 35.42) * mm});
            skLineSegment(sketch, "E13.35.3", {"start": v(6.6, 37.4) * mm, "end": v(6.44, 36.17) * mm});
            skPoint(sketch, "E13.35.4", {"position": v(3.32, 37.96) * mm});
            skPoint(sketch, "E13.35.5", {"position": v(3.04, 35.85) * mm});
            skPoint(sketch, "E13.35.6", {"position": v(5.89, 39.77) * mm});
            skArc(sketch, "E13.35.7", {"start": v(6.59, 37.66) * mm, "mid": v(6.34, 38.6) * mm, "end": v(6, 39.52) * mm});
            skPoint(sketch, "E13.35.8", {"position": v(6.62, 37.52) * mm});
            skPoint(sketch, "E13.35.9", {"position": v(4.6, 39.94) * mm});
            skArc(sketch, "E13.35.10", {"start": v(6.44, 36.17) * mm, "mid": v(6.58, 35.6) * mm, "end": v(7.07, 35.28) * mm});
            skArc(sketch, "E13.35.11", {"start": v(2.3, 35.9) * mm, "mid": v(2.86, 36.09) * mm, "end": v(3.14, 36.6) * mm});
            skArc(sketch, "E13.35.12", {"start": v(6, 39.52) * mm, "mid": v(5.85, 39.72) * mm, "end": v(5.62, 39.82) * mm});
            skLineSegment(sketch, "E13.35.13", {"start": v(5.62, 39.82) * mm, "end": v(5.25, 39.89) * mm});
            skLineSegment(sketch, "E13.35.14", {"start": v(4.87, 39.92) * mm, "end": v(5.25, 39.89) * mm});
            skArc(sketch, "E13.35.15", {"start": v(6.6, 37.4) * mm, "mid": v(6.6, 37.52) * mm, "end": v(6.59, 37.66) * mm});
            skArc(sketch, "E13.35.16", {"start": v(3.38, 38.08) * mm, "mid": v(3.33, 37.95) * mm, "end": v(3.3, 37.82) * mm});
            skArc(sketch, "E13.35.17", {"start": v(4.87, 39.92) * mm, "mid": v(4.63, 39.88) * mm, "end": v(4.43, 39.73) * mm});
            skSolve(sketch);
        }
        {
            var Q0;
            Q0 = qSketchRegion(id + "F0", true);
            extrude(context, id + "F1", {"entities" : qUnion([Q0]), "depth" : 6.35 * mm});
        }
        {
            var Q0;
            Q0=sQuery(id+"F0.wireOp",VERTEX,"E0.center");
            var Q1;
            Q1=makeQuery(id+"F1.opExtrude","SWEPT_BODY",BODY,{"disambiguationData":[OSD([sQuery(id+"F0.wireOp",EDGE,"E0"),sQuery(id+"F0.wireOp",EDGE,"E1.trimOffspring"),sQuery(id+"F0.wireOp",EDGE,"E2"),sQuery(id+"F0.wireOp",EDGE,"E3"),sQuery(id+"F0.wireOp",EDGE,"E4.MirrorCS"),sQuery(id+"F0.wireOp",EDGE,"E5.MirrorCS"),sQuery(id+"F0.wireOp",EDGE,"E6.MirrorCS"),sQuery(id+"F0.wireOp",EDGE,"E7.filletArc"),sQuery(id+"F0.wireOp",EDGE,"E8.filletArc"),sQuery(id+"F0.wireOp",EDGE,"E9.filletArc"),sQuery(id+"F0.wireOp",EDGE,"E10.filletArc"),sQuery(id+"F0.wireOp",EDGE,"E11.filletArc"),sQuery(id+"F0.wireOp",EDGE,"E12.filletArc"),sQuery(id+"F0.wireOp",EDGE,"E13.1.0"),sQuery(id+"F0.wireOp",EDGE,"E13.1.1"),sQuery(id+"F0.wireOp",EDGE,"E13.1.3"),sQuery(id+"F0.wireOp",EDGE,"E13.1.7"),sQuery(id+"F0.wireOp",EDGE,"E13.1.10"),sQuery(id+"F0.wireOp",EDGE,"E13.1.11"),sQuery(id+"F0.wireOp",EDGE,"E13.1.12"),sQuery(id+"F0.wireOp",EDGE,"E13.1.13"),sQuery(id+"F0.wireOp",EDGE,"E13.1.14"),sQuery(id+"F0.wireOp",EDGE,"E13.1.15"),sQuery(id+"F0.wireOp",EDGE,"E13.1.16"),sQuery(id+"F0.wireOp",EDGE,"E13.1.17"),sQuery(id+"F0.wireOp",EDGE,"E13.2.0"),sQuery(id+"F0.wireOp",EDGE,"E13.2.1"),sQuery(id+"F0.wireOp",EDGE,"E13.2.3"),sQuery(id+"F0.wireOp",EDGE,"E13.2.7"),sQuery(id+"F0.wireOp",EDGE,"E13.2.10"),sQuery(id+"F0.wireOp",EDGE,"E13.2.11"),sQuery(id+"F0.wireOp",EDGE,"E13.2.12"),sQuery(id+"F0.wireOp",EDGE,"E13.2.13"),sQuery(id+"F0.wireOp",EDGE,"E13.2.14"),sQuery(id+"F0.wireOp",EDGE,"E13.2.15"),sQuery(id+"F0.wireOp",EDGE,"E13.2.16"),sQuery(id+"F0.wireOp",EDGE,"E13.2.17"),sQuery(id+"F0.wireOp",EDGE,"E13.3.0"),sQuery(id+"F0.wireOp",EDGE,"E13.3.1"),sQuery(id+"F0.wireOp",EDGE,"E13.3.3"),sQuery(id+"F0.wireOp",EDGE,"E13.3.7"),sQuery(id+"F0.wireOp",EDGE,"E13.3.10"),sQuery(id+"F0.wireOp",EDGE,"E13.3.11"),sQuery(id+"F0.wireOp",EDGE,"E13.3.12"),sQuery(id+"F0.wireOp",EDGE,"E13.3.13"),sQuery(id+"F0.wireOp",EDGE,"E13.3.14"),sQuery(id+"F0.wireOp",EDGE,"E13.3.15"),sQuery(id+"F0.wireOp",EDGE,"E13.3.16"),sQuery(id+"F0.wireOp",EDGE,"E13.3.17"),sQuery(id+"F0.wireOp",EDGE,"E13.4.0"),sQuery(id+"F0.wireOp",EDGE,"E13.4.1"),sQuery(id+"F0.wireOp",EDGE,"E13.4.3"),sQuery(id+"F0.wireOp",EDGE,"E13.4.7"),sQuery(id+"F0.wireOp",EDGE,"E13.4.10"),sQuery(id+"F0.wireOp",EDGE,"E13.4.11"),sQuery(id+"F0.wireOp",EDGE,"E13.4.12"),sQuery(id+"F0.wireOp",EDGE,"E13.4.13"),sQuery(id+"F0.wireOp",EDGE,"E13.4.14"),sQuery(id+"F0.wireOp",EDGE,"E13.4.15"),sQuery(id+"F0.wireOp",EDGE,"E13.4.16"),sQuery(id+"F0.wireOp",EDGE,"E13.4.17"),sQuery(id+"F0.wireOp",EDGE,"E13.5.0"),sQuery(id+"F0.wireOp",EDGE,"E13.5.1"),sQuery(id+"F0.wireOp",EDGE,"E13.5.3"),sQuery(id+"F0.wireOp",EDGE,"E13.5.7"),sQuery(id+"F0.wireOp",EDGE,"E13.5.10"),sQuery(id+"F0.wireOp",EDGE,"E13.5.11"),sQuery(id+"F0.wireOp",EDGE,"E13.5.12"),sQuery(id+"F0.wireOp",EDGE,"E13.5.13"),sQuery(id+"F0.wireOp",EDGE,"E13.5.14"),sQuery(id+"F0.wireOp",EDGE,"E13.5.15"),sQuery(id+"F0.wireOp",EDGE,"E13.5.16"),sQuery(id+"F0.wireOp",EDGE,"E13.5.17"),sQuery(id+"F0.wireOp",EDGE,"E13.6.0"),sQuery(id+"F0.wireOp",EDGE,"E13.6.1"),sQuery(id+"F0.wireOp",EDGE,"E13.6.3"),sQuery(id+"F0.wireOp",EDGE,"E13.6.7"),sQuery(id+"F0.wireOp",EDGE,"E13.6.10"),sQuery(id+"F0.wireOp",EDGE,"E13.6.11"),sQuery(id+"F0.wireOp",EDGE,"E13.6.12"),sQuery(id+"F0.wireOp",EDGE,"E13.6.13"),sQuery(id+"F0.wireOp",EDGE,"E13.6.14"),sQuery(id+"F0.wireOp",EDGE,"E13.6.15"),sQuery(id+"F0.wireOp",EDGE,"E13.6.16"),sQuery(id+"F0.wireOp",EDGE,"E13.6.17"),sQuery(id+"F0.wireOp",EDGE,"E13.7.0"),sQuery(id+"F0.wireOp",EDGE,"E13.7.1"),sQuery(id+"F0.wireOp",EDGE,"E13.7.3"),sQuery(id+"F0.wireOp",EDGE,"E13.7.7"),sQuery(id+"F0.wireOp",EDGE,"E13.7.10"),sQuery(id+"F0.wireOp",EDGE,"E13.7.11"),sQuery(id+"F0.wireOp",EDGE,"E13.7.12"),sQuery(id+"F0.wireOp",EDGE,"E13.7.13"),sQuery(id+"F0.wireOp",EDGE,"E13.7.14"),sQuery(id+"F0.wireOp",EDGE,"E13.7.15"),sQuery(id+"F0.wireOp",EDGE,"E13.7.16"),sQuery(id+"F0.wireOp",EDGE,"E13.7.17"),sQuery(id+"F0.wireOp",EDGE,"E13.8.0"),sQuery(id+"F0.wireOp",EDGE,"E13.8.1"),sQuery(id+"F0.wireOp",EDGE,"E13.8.3"),sQuery(id+"F0.wireOp",EDGE,"E13.8.7"),sQuery(id+"F0.wireOp",EDGE,"E13.8.10"),sQuery(id+"F0.wireOp",EDGE,"E13.8.11"),sQuery(id+"F0.wireOp",EDGE,"E13.8.12"),sQuery(id+"F0.wireOp",EDGE,"E13.8.13"),sQuery(id+"F0.wireOp",EDGE,"E13.8.14"),sQuery(id+"F0.wireOp",EDGE,"E13.8.15"),sQuery(id+"F0.wireOp",EDGE,"E13.8.16"),sQuery(id+"F0.wireOp",EDGE,"E13.8.17"),sQuery(id+"F0.wireOp",EDGE,"E13.9.0"),sQuery(id+"F0.wireOp",EDGE,"E13.9.1"),sQuery(id+"F0.wireOp",EDGE,"E13.9.3"),sQuery(id+"F0.wireOp",EDGE,"E13.9.7"),sQuery(id+"F0.wireOp",EDGE,"E13.9.10"),sQuery(id+"F0.wireOp",EDGE,"E13.9.11"),sQuery(id+"F0.wireOp",EDGE,"E13.9.12"),sQuery(id+"F0.wireOp",EDGE,"E13.9.13"),sQuery(id+"F0.wireOp",EDGE,"E13.9.14"),sQuery(id+"F0.wireOp",EDGE,"E13.9.15"),sQuery(id+"F0.wireOp",EDGE,"E13.9.16"),sQuery(id+"F0.wireOp",EDGE,"E13.9.17"),sQuery(id+"F0.wireOp",EDGE,"E13.10.0"),sQuery(id+"F0.wireOp",EDGE,"E13.10.1"),sQuery(id+"F0.wireOp",EDGE,"E13.10.3"),sQuery(id+"F0.wireOp",EDGE,"E13.10.7"),sQuery(id+"F0.wireOp",EDGE,"E13.10.10"),sQuery(id+"F0.wireOp",EDGE,"E13.10.11"),sQuery(id+"F0.wireOp",EDGE,"E13.10.12"),sQuery(id+"F0.wireOp",EDGE,"E13.10.13"),sQuery(id+"F0.wireOp",EDGE,"E13.10.14"),sQuery(id+"F0.wireOp",EDGE,"E13.10.15"),sQuery(id+"F0.wireOp",EDGE,"E13.10.16"),sQuery(id+"F0.wireOp",EDGE,"E13.10.17"),sQuery(id+"F0.wireOp",EDGE,"E13.11.0"),sQuery(id+"F0.wireOp",EDGE,"E13.11.1"),sQuery(id+"F0.wireOp",EDGE,"E13.11.3"),sQuery(id+"F0.wireOp",EDGE,"E13.11.7"),sQuery(id+"F0.wireOp",EDGE,"E13.11.10"),sQuery(id+"F0.wireOp",EDGE,"E13.11.11"),sQuery(id+"F0.wireOp",EDGE,"E13.11.12"),sQuery(id+"F0.wireOp",EDGE,"E13.11.13"),sQuery(id+"F0.wireOp",EDGE,"E13.11.14"),sQuery(id+"F0.wireOp",EDGE,"E13.11.15"),sQuery(id+"F0.wireOp",EDGE,"E13.11.16"),sQuery(id+"F0.wireOp",EDGE,"E13.11.17"),sQuery(id+"F0.wireOp",EDGE,"E13.12.0"),sQuery(id+"F0.wireOp",EDGE,"E13.12.1"),sQuery(id+"F0.wireOp",EDGE,"E13.12.3"),sQuery(id+"F0.wireOp",EDGE,"E13.12.7"),sQuery(id+"F0.wireOp",EDGE,"E13.12.10"),sQuery(id+"F0.wireOp",EDGE,"E13.12.11"),sQuery(id+"F0.wireOp",EDGE,"E13.12.12"),sQuery(id+"F0.wireOp",EDGE,"E13.12.13"),sQuery(id+"F0.wireOp",EDGE,"E13.12.14"),sQuery(id+"F0.wireOp",EDGE,"E13.12.15"),sQuery(id+"F0.wireOp",EDGE,"E13.12.16"),sQuery(id+"F0.wireOp",EDGE,"E13.12.17"),sQuery(id+"F0.wireOp",EDGE,"E13.13.0"),sQuery(id+"F0.wireOp",EDGE,"E13.13.1"),sQuery(id+"F0.wireOp",EDGE,"E13.13.3"),sQuery(id+"F0.wireOp",EDGE,"E13.13.7"),sQuery(id+"F0.wireOp",EDGE,"E13.13.10"),sQuery(id+"F0.wireOp",EDGE,"E13.13.11"),sQuery(id+"F0.wireOp",EDGE,"E13.13.12"),sQuery(id+"F0.wireOp",EDGE,"E13.13.13"),sQuery(id+"F0.wireOp",EDGE,"E13.13.14"),sQuery(id+"F0.wireOp",EDGE,"E13.13.15"),sQuery(id+"F0.wireOp",EDGE,"E13.13.16"),sQuery(id+"F0.wireOp",EDGE,"E13.13.17"),sQuery(id+"F0.wireOp",EDGE,"E13.14.0"),sQuery(id+"F0.wireOp",EDGE,"E13.14.1"),sQuery(id+"F0.wireOp",EDGE,"E13.14.3"),sQuery(id+"F0.wireOp",EDGE,"E13.14.7"),sQuery(id+"F0.wireOp",EDGE,"E13.14.10"),sQuery(id+"F0.wireOp",EDGE,"E13.14.11"),sQuery(id+"F0.wireOp",EDGE,"E13.14.12"),sQuery(id+"F0.wireOp",EDGE,"E13.14.13"),sQuery(id+"F0.wireOp",EDGE,"E13.14.14"),sQuery(id+"F0.wireOp",EDGE,"E13.14.15"),sQuery(id+"F0.wireOp",EDGE,"E13.14.16"),sQuery(id+"F0.wireOp",EDGE,"E13.14.17"),sQuery(id+"F0.wireOp",EDGE,"E13.15.0"),sQuery(id+"F0.wireOp",EDGE,"E13.15.1"),sQuery(id+"F0.wireOp",EDGE,"E13.15.3"),sQuery(id+"F0.wireOp",EDGE,"E13.15.7"),sQuery(id+"F0.wireOp",EDGE,"E13.15.10"),sQuery(id+"F0.wireOp",EDGE,"E13.15.11"),sQuery(id+"F0.wireOp",EDGE,"E13.15.12"),sQuery(id+"F0.wireOp",EDGE,"E13.15.13"),sQuery(id+"F0.wireOp",EDGE,"E13.15.14"),sQuery(id+"F0.wireOp",EDGE,"E13.15.15"),sQuery(id+"F0.wireOp",EDGE,"E13.15.16"),sQuery(id+"F0.wireOp",EDGE,"E13.15.17"),sQuery(id+"F0.wireOp",EDGE,"E13.16.0"),sQuery(id+"F0.wireOp",EDGE,"E13.16.1"),sQuery(id+"F0.wireOp",EDGE,"E13.16.3"),sQuery(id+"F0.wireOp",EDGE,"E13.16.7"),sQuery(id+"F0.wireOp",EDGE,"E13.16.10"),sQuery(id+"F0.wireOp",EDGE,"E13.16.11"),sQuery(id+"F0.wireOp",EDGE,"E13.16.12"),sQuery(id+"F0.wireOp",EDGE,"E13.16.13"),sQuery(id+"F0.wireOp",EDGE,"E13.16.14"),sQuery(id+"F0.wireOp",EDGE,"E13.16.15"),sQuery(id+"F0.wireOp",EDGE,"E13.16.16"),sQuery(id+"F0.wireOp",EDGE,"E13.16.17"),sQuery(id+"F0.wireOp",EDGE,"E13.17.0"),sQuery(id+"F0.wireOp",EDGE,"E13.17.1"),sQuery(id+"F0.wireOp",EDGE,"E13.17.3"),sQuery(id+"F0.wireOp",EDGE,"E13.17.7"),sQuery(id+"F0.wireOp",EDGE,"E13.17.10"),sQuery(id+"F0.wireOp",EDGE,"E13.17.11"),sQuery(id+"F0.wireOp",EDGE,"E13.17.12"),sQuery(id+"F0.wireOp",EDGE,"E13.17.13"),sQuery(id+"F0.wireOp",EDGE,"E13.17.14"),sQuery(id+"F0.wireOp",EDGE,"E13.17.15"),sQuery(id+"F0.wireOp",EDGE,"E13.17.16"),sQuery(id+"F0.wireOp",EDGE,"E13.17.17"),sQuery(id+"F0.wireOp",EDGE,"E13.18.0"),sQuery(id+"F0.wireOp",EDGE,"E13.18.1"),sQuery(id+"F0.wireOp",EDGE,"E13.18.3"),sQuery(id+"F0.wireOp",EDGE,"E13.18.7"),sQuery(id+"F0.wireOp",EDGE,"E13.18.10"),sQuery(id+"F0.wireOp",EDGE,"E13.18.11"),sQuery(id+"F0.wireOp",EDGE,"E13.18.12"),sQuery(id+"F0.wireOp",EDGE,"E13.18.13"),sQuery(id+"F0.wireOp",EDGE,"E13.18.14"),sQuery(id+"F0.wireOp",EDGE,"E13.18.15"),sQuery(id+"F0.wireOp",EDGE,"E13.18.16"),sQuery(id+"F0.wireOp",EDGE,"E13.18.17"),sQuery(id+"F0.wireOp",EDGE,"E13.19.0"),sQuery(id+"F0.wireOp",EDGE,"E13.19.1"),sQuery(id+"F0.wireOp",EDGE,"E13.19.3"),sQuery(id+"F0.wireOp",EDGE,"E13.19.7"),sQuery(id+"F0.wireOp",EDGE,"E13.19.10"),sQuery(id+"F0.wireOp",EDGE,"E13.19.11"),sQuery(id+"F0.wireOp",EDGE,"E13.19.12"),sQuery(id+"F0.wireOp",EDGE,"E13.19.13"),sQuery(id+"F0.wireOp",EDGE,"E13.19.14"),sQuery(id+"F0.wireOp",EDGE,"E13.19.15"),sQuery(id+"F0.wireOp",EDGE,"E13.19.16"),sQuery(id+"F0.wireOp",EDGE,"E13.19.17"),sQuery(id+"F0.wireOp",EDGE,"E13.20.0"),sQuery(id+"F0.wireOp",EDGE,"E13.20.1"),sQuery(id+"F0.wireOp",EDGE,"E13.20.3"),sQuery(id+"F0.wireOp",EDGE,"E13.20.7"),sQuery(id+"F0.wireOp",EDGE,"E13.20.10"),sQuery(id+"F0.wireOp",EDGE,"E13.20.11"),sQuery(id+"F0.wireOp",EDGE,"E13.20.12"),sQuery(id+"F0.wireOp",EDGE,"E13.20.13"),sQuery(id+"F0.wireOp",EDGE,"E13.20.14"),sQuery(id+"F0.wireOp",EDGE,"E13.20.15"),sQuery(id+"F0.wireOp",EDGE,"E13.20.16"),sQuery(id+"F0.wireOp",EDGE,"E13.20.17"),sQuery(id+"F0.wireOp",EDGE,"E13.21.0"),sQuery(id+"F0.wireOp",EDGE,"E13.21.1"),sQuery(id+"F0.wireOp",EDGE,"E13.21.3"),sQuery(id+"F0.wireOp",EDGE,"E13.21.7"),sQuery(id+"F0.wireOp",EDGE,"E13.21.10"),sQuery(id+"F0.wireOp",EDGE,"E13.21.11"),sQuery(id+"F0.wireOp",EDGE,"E13.21.12"),sQuery(id+"F0.wireOp",EDGE,"E13.21.13"),sQuery(id+"F0.wireOp",EDGE,"E13.21.14"),sQuery(id+"F0.wireOp",EDGE,"E13.21.15"),sQuery(id+"F0.wireOp",EDGE,"E13.21.16"),sQuery(id+"F0.wireOp",EDGE,"E13.21.17"),sQuery(id+"F0.wireOp",EDGE,"E13.22.0"),sQuery(id+"F0.wireOp",EDGE,"E13.22.1"),sQuery(id+"F0.wireOp",EDGE,"E13.22.3"),sQuery(id+"F0.wireOp",EDGE,"E13.22.7"),sQuery(id+"F0.wireOp",EDGE,"E13.22.10"),sQuery(id+"F0.wireOp",EDGE,"E13.22.11"),sQuery(id+"F0.wireOp",EDGE,"E13.22.12"),sQuery(id+"F0.wireOp",EDGE,"E13.22.13"),sQuery(id+"F0.wireOp",EDGE,"E13.22.14"),sQuery(id+"F0.wireOp",EDGE,"E13.22.15"),sQuery(id+"F0.wireOp",EDGE,"E13.22.16"),sQuery(id+"F0.wireOp",EDGE,"E13.22.17"),sQuery(id+"F0.wireOp",EDGE,"E13.23.0"),sQuery(id+"F0.wireOp",EDGE,"E13.23.1"),sQuery(id+"F0.wireOp",EDGE,"E13.23.3"),sQuery(id+"F0.wireOp",EDGE,"E13.23.7"),sQuery(id+"F0.wireOp",EDGE,"E13.23.10"),sQuery(id+"F0.wireOp",EDGE,"E13.23.11"),sQuery(id+"F0.wireOp",EDGE,"E13.23.12"),sQuery(id+"F0.wireOp",EDGE,"E13.23.13"),sQuery(id+"F0.wireOp",EDGE,"E13.23.14"),sQuery(id+"F0.wireOp",EDGE,"E13.23.15"),sQuery(id+"F0.wireOp",EDGE,"E13.23.16"),sQuery(id+"F0.wireOp",EDGE,"E13.23.17"),sQuery(id+"F0.wireOp",EDGE,"E13.24.0"),sQuery(id+"F0.wireOp",EDGE,"E13.24.1"),sQuery(id+"F0.wireOp",EDGE,"E13.24.3"),sQuery(id+"F0.wireOp",EDGE,"E13.24.7"),sQuery(id+"F0.wireOp",EDGE,"E13.24.10"),sQuery(id+"F0.wireOp",EDGE,"E13.24.11"),sQuery(id+"F0.wireOp",EDGE,"E13.24.12"),sQuery(id+"F0.wireOp",EDGE,"E13.24.13"),sQuery(id+"F0.wireOp",EDGE,"E13.24.14"),sQuery(id+"F0.wireOp",EDGE,"E13.24.15"),sQuery(id+"F0.wireOp",EDGE,"E13.24.16"),sQuery(id+"F0.wireOp",EDGE,"E13.24.17"),sQuery(id+"F0.wireOp",EDGE,"E13.25.0"),sQuery(id+"F0.wireOp",EDGE,"E13.25.1"),sQuery(id+"F0.wireOp",EDGE,"E13.25.3"),sQuery(id+"F0.wireOp",EDGE,"E13.25.7"),sQuery(id+"F0.wireOp",EDGE,"E13.25.10"),sQuery(id+"F0.wireOp",EDGE,"E13.25.11"),sQuery(id+"F0.wireOp",EDGE,"E13.25.12"),sQuery(id+"F0.wireOp",EDGE,"E13.25.13"),sQuery(id+"F0.wireOp",EDGE,"E13.25.14"),sQuery(id+"F0.wireOp",EDGE,"E13.25.15"),sQuery(id+"F0.wireOp",EDGE,"E13.25.16"),sQuery(id+"F0.wireOp",EDGE,"E13.25.17"),sQuery(id+"F0.wireOp",EDGE,"E13.26.0"),sQuery(id+"F0.wireOp",EDGE,"E13.26.1"),sQuery(id+"F0.wireOp",EDGE,"E13.26.3"),sQuery(id+"F0.wireOp",EDGE,"E13.26.7"),sQuery(id+"F0.wireOp",EDGE,"E13.26.10"),sQuery(id+"F0.wireOp",EDGE,"E13.26.11"),sQuery(id+"F0.wireOp",EDGE,"E13.26.12"),sQuery(id+"F0.wireOp",EDGE,"E13.26.13"),sQuery(id+"F0.wireOp",EDGE,"E13.26.14"),sQuery(id+"F0.wireOp",EDGE,"E13.26.15"),sQuery(id+"F0.wireOp",EDGE,"E13.26.16"),sQuery(id+"F0.wireOp",EDGE,"E13.26.17"),sQuery(id+"F0.wireOp",EDGE,"E13.27.0"),sQuery(id+"F0.wireOp",EDGE,"E13.27.1"),sQuery(id+"F0.wireOp",EDGE,"E13.27.3"),sQuery(id+"F0.wireOp",EDGE,"E13.27.7"),sQuery(id+"F0.wireOp",EDGE,"E13.27.10"),sQuery(id+"F0.wireOp",EDGE,"E13.27.11"),sQuery(id+"F0.wireOp",EDGE,"E13.27.12"),sQuery(id+"F0.wireOp",EDGE,"E13.27.13"),sQuery(id+"F0.wireOp",EDGE,"E13.27.14"),sQuery(id+"F0.wireOp",EDGE,"E13.27.15"),sQuery(id+"F0.wireOp",EDGE,"E13.27.16"),sQuery(id+"F0.wireOp",EDGE,"E13.27.17"),sQuery(id+"F0.wireOp",EDGE,"E13.28.0"),sQuery(id+"F0.wireOp",EDGE,"E13.28.1"),sQuery(id+"F0.wireOp",EDGE,"E13.28.3"),sQuery(id+"F0.wireOp",EDGE,"E13.28.7"),sQuery(id+"F0.wireOp",EDGE,"E13.28.10"),sQuery(id+"F0.wireOp",EDGE,"E13.28.11"),sQuery(id+"F0.wireOp",EDGE,"E13.28.12"),sQuery(id+"F0.wireOp",EDGE,"E13.28.13"),sQuery(id+"F0.wireOp",EDGE,"E13.28.14"),sQuery(id+"F0.wireOp",EDGE,"E13.28.15"),sQuery(id+"F0.wireOp",EDGE,"E13.28.16"),sQuery(id+"F0.wireOp",EDGE,"E13.28.17"),sQuery(id+"F0.wireOp",EDGE,"E13.29.0"),sQuery(id+"F0.wireOp",EDGE,"E13.29.1"),sQuery(id+"F0.wireOp",EDGE,"E13.29.3"),sQuery(id+"F0.wireOp",EDGE,"E13.29.7"),sQuery(id+"F0.wireOp",EDGE,"E13.29.10"),sQuery(id+"F0.wireOp",EDGE,"E13.29.11"),sQuery(id+"F0.wireOp",EDGE,"E13.29.12"),sQuery(id+"F0.wireOp",EDGE,"E13.29.13"),sQuery(id+"F0.wireOp",EDGE,"E13.29.14"),sQuery(id+"F0.wireOp",EDGE,"E13.29.15"),sQuery(id+"F0.wireOp",EDGE,"E13.29.16"),sQuery(id+"F0.wireOp",EDGE,"E13.29.17"),sQuery(id+"F0.wireOp",EDGE,"E13.30.0"),sQuery(id+"F0.wireOp",EDGE,"E13.30.1"),sQuery(id+"F0.wireOp",EDGE,"E13.30.3"),sQuery(id+"F0.wireOp",EDGE,"E13.30.7"),sQuery(id+"F0.wireOp",EDGE,"E13.30.10"),sQuery(id+"F0.wireOp",EDGE,"E13.30.11"),sQuery(id+"F0.wireOp",EDGE,"E13.30.12"),sQuery(id+"F0.wireOp",EDGE,"E13.30.13"),sQuery(id+"F0.wireOp",EDGE,"E13.30.14"),sQuery(id+"F0.wireOp",EDGE,"E13.30.15"),sQuery(id+"F0.wireOp",EDGE,"E13.30.16"),sQuery(id+"F0.wireOp",EDGE,"E13.30.17"),sQuery(id+"F0.wireOp",EDGE,"E13.31.0"),sQuery(id+"F0.wireOp",EDGE,"E13.31.1"),sQuery(id+"F0.wireOp",EDGE,"E13.31.3"),sQuery(id+"F0.wireOp",EDGE,"E13.31.7"),sQuery(id+"F0.wireOp",EDGE,"E13.31.10"),sQuery(id+"F0.wireOp",EDGE,"E13.31.11"),sQuery(id+"F0.wireOp",EDGE,"E13.31.12"),sQuery(id+"F0.wireOp",EDGE,"E13.31.13"),sQuery(id+"F0.wireOp",EDGE,"E13.31.14"),sQuery(id+"F0.wireOp",EDGE,"E13.31.15"),sQuery(id+"F0.wireOp",EDGE,"E13.31.16"),sQuery(id+"F0.wireOp",EDGE,"E13.31.17"),sQuery(id+"F0.wireOp",EDGE,"E13.32.0"),sQuery(id+"F0.wireOp",EDGE,"E13.32.1"),sQuery(id+"F0.wireOp",EDGE,"E13.32.3"),sQuery(id+"F0.wireOp",EDGE,"E13.32.7"),sQuery(id+"F0.wireOp",EDGE,"E13.32.10"),sQuery(id+"F0.wireOp",EDGE,"E13.32.11"),sQuery(id+"F0.wireOp",EDGE,"E13.32.12"),sQuery(id+"F0.wireOp",EDGE,"E13.32.13"),sQuery(id+"F0.wireOp",EDGE,"E13.32.14"),sQuery(id+"F0.wireOp",EDGE,"E13.32.15"),sQuery(id+"F0.wireOp",EDGE,"E13.32.16"),sQuery(id+"F0.wireOp",EDGE,"E13.32.17"),sQuery(id+"F0.wireOp",EDGE,"E13.33.0"),sQuery(id+"F0.wireOp",EDGE,"E13.33.1"),sQuery(id+"F0.wireOp",EDGE,"E13.33.3"),sQuery(id+"F0.wireOp",EDGE,"E13.33.7"),sQuery(id+"F0.wireOp",EDGE,"E13.33.10"),sQuery(id+"F0.wireOp",EDGE,"E13.33.11"),sQuery(id+"F0.wireOp",EDGE,"E13.33.12"),sQuery(id+"F0.wireOp",EDGE,"E13.33.13"),sQuery(id+"F0.wireOp",EDGE,"E13.33.14"),sQuery(id+"F0.wireOp",EDGE,"E13.33.15"),sQuery(id+"F0.wireOp",EDGE,"E13.33.16"),sQuery(id+"F0.wireOp",EDGE,"E13.33.17"),sQuery(id+"F0.wireOp",EDGE,"E13.34.0"),sQuery(id+"F0.wireOp",EDGE,"E13.34.1"),sQuery(id+"F0.wireOp",EDGE,"E13.34.3"),sQuery(id+"F0.wireOp",EDGE,"E13.34.7"),sQuery(id+"F0.wireOp",EDGE,"E13.34.10"),sQuery(id+"F0.wireOp",EDGE,"E13.34.11"),sQuery(id+"F0.wireOp",EDGE,"E13.34.12"),sQuery(id+"F0.wireOp",EDGE,"E13.34.13"),sQuery(id+"F0.wireOp",EDGE,"E13.34.14"),sQuery(id+"F0.wireOp",EDGE,"E13.34.15"),sQuery(id+"F0.wireOp",EDGE,"E13.34.16"),sQuery(id+"F0.wireOp",EDGE,"E13.34.17"),sQuery(id+"F0.wireOp",EDGE,"E13.35.0"),sQuery(id+"F0.wireOp",EDGE,"E13.35.1"),sQuery(id+"F0.wireOp",EDGE,"E13.35.3"),sQuery(id+"F0.wireOp",EDGE,"E13.35.7"),sQuery(id+"F0.wireOp",EDGE,"E13.35.10"),sQuery(id+"F0.wireOp",EDGE,"E13.35.11"),sQuery(id+"F0.wireOp",EDGE,"E13.35.12"),sQuery(id+"F0.wireOp",EDGE,"E13.35.13"),sQuery(id+"F0.wireOp",EDGE,"E13.35.14"),sQuery(id+"F0.wireOp",EDGE,"E13.35.15"),sQuery(id+"F0.wireOp",EDGE,"E13.35.16"),sQuery(id+"F0.wireOp",EDGE,"E13.35.17")])]});
            hole(context, id + "F2", {"style" : HoleStyle.SIMPLE, "endStyle" : HoleEndStyle.BLIND, "oppositeDirection" : true, "holeDiameter" : 12.7 * mm, "holeDepth" : 50.8 * mm, "tappedDepth" : 12.7 * mm, "tapClearance" : 3, "locations" : qUnion([Q0]), "scope" : qUnion([Q1])});
        }
    });
